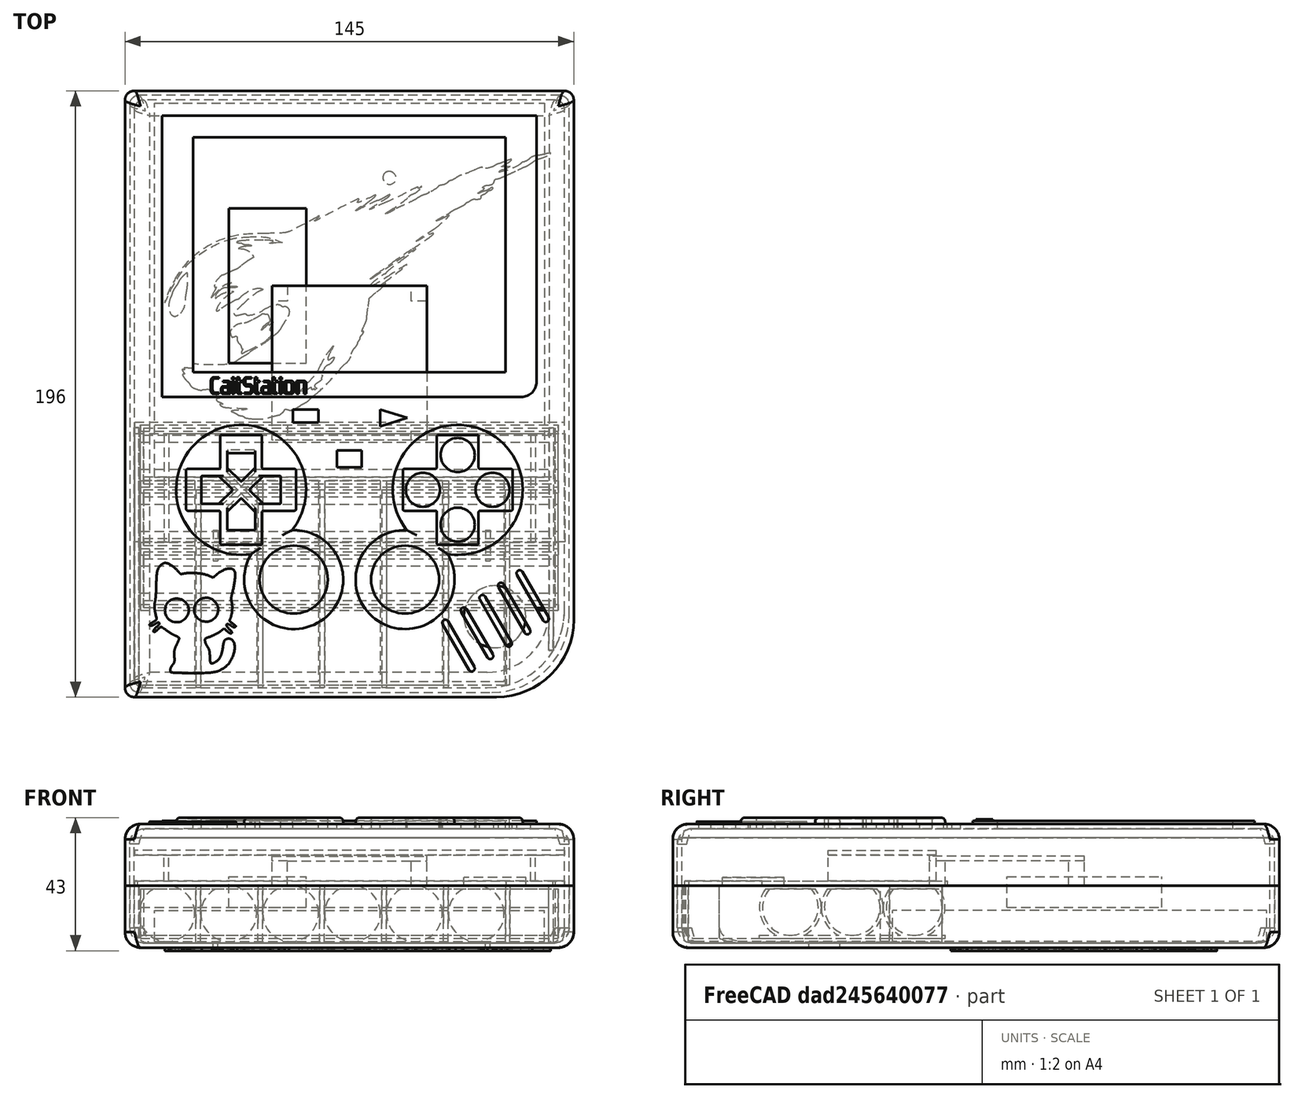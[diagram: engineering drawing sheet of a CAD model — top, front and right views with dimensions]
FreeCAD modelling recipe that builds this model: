
FCSTD DOCUMENT  (FreeCAD 0.15R4671 (Git))
Label: ps2-gb-small
License: All rights reserved
LicenseURL: http://en.wikipedia.org/wiki/All_rights_reserved
objects: Sketcher::SketchObject×33, PartDesign::Pad×32, Part::Cut×24, Part::MultiFuse×15, App::DocumentObjectGroup×15, PartDesign::Fillet×10, Part::Cylinder×9, Part::Feature×8, Part::Extrusion×6, Part::Box×5, Part::FeaturePython×2, Part::Part2DObjectPython×1
note: 177 computed .brp shape members not serialized (recipe doc carries the construction recipe); baked Part::Feature solids carry a one-line shape summary decoded from their .brp

FEATURE [Sketcher::SketchObject] Sketch001  label="Face-sketch"
  sketch-geometry (13):
    g0: LineSegment StartX=-69.5 StartY=88 StartZ=0 EndX=69.5 EndY=88 EndZ=0
    g1: LineSegment StartX=72.5 StartY=85 StartZ=0 EndX=72.5 EndY=-83 EndZ=0
    g2: LineSegment StartX=47.5 StartY=-108 StartZ=0 EndX=-69.5 EndY=-108 EndZ=0
    g3: LineSegment StartX=-72.5 StartY=-105 StartZ=0 EndX=-72.5 EndY=85 EndZ=0
    g4: LineSegment StartX=-50.5 StartY=73 StartZ=0 EndX=50.5 EndY=73 EndZ=0
    g5: LineSegment StartX=50.5 StartY=73 StartZ=0 EndX=50.5 EndY=-3 EndZ=0
    g6: LineSegment StartX=50.5 StartY=-3 StartZ=0 EndX=-50.5 EndY=-3 EndZ=0
    g7: LineSegment StartX=-50.5 StartY=-3 StartZ=0 EndX=-50.5 EndY=73 EndZ=0
    g8: ArcOfCircle CenterX=47.5 CenterY=-83 CenterZ=0 NormalX=0 NormalY=0 NormalZ=1 Radius=25 StartAngle=4.71239 EndAngle=6.28319
    g9: ArcOfCircle CenterX=-69.5 CenterY=-105 CenterZ=0 NormalX=0 NormalY=0 NormalZ=1 Radius=3 StartAngle=3.14159 EndAngle=4.71239
    g10: ArcOfCircle CenterX=69.5 CenterY=85 CenterZ=0 NormalX=0 NormalY=0 NormalZ=1 Radius=3 StartAngle=0 EndAngle=1.5708
    g11: ArcOfCircle CenterX=-69.5 CenterY=85 CenterZ=0 NormalX=0 NormalY=0 NormalZ=1 Radius=3 StartAngle=1.5708 EndAngle=3.14159
    g12: GeomPoint [constr] X=-72.5 Y=88 Z=0
  constraints (34):
    c: Horizontal(g0)
    c: Horizontal(g2)
    c: Vertical(g1)
    c: Vertical(g3)
    c: Coincident(g4,g5)
    c: Coincident(g5,g6)
    c: Coincident(g6,g7)
    c: Coincident(g7,g4)
    c: Horizontal(g4)
    c: Horizontal(g6)
    c: Vertical(g5)
    c: Vertical(g7)
    c: DistanceX(g4) = 101
    c: DistanceY(g7) = 76
    c: Tangent(g1,g8) = 1.5708
    c: Tangent(g2,g8) = 1.5708
    c: Radius(g8) = 25
    c: Tangent(g2,g9) = 1.5708
    c: Tangent(g3,g9) = 1.5708
    c: Tangent(g0,g10) = 1.5708
    c: Tangent(g1,g10) = 1.5708
    c: Tangent(g0,g11) = 1.5708
    c: Tangent(g3,g11) = 1.5708
    c: Radius(g11) = 3
    c: Radius(g10) = 3
    c: Equal(g10,g9)
    c: DistanceY(g3) = 190
    c: DistanceX(g0) = 139
    c: DistanceX(g12,g0) = 3
    c: DistanceY(g12,g3) = -3
    c: DistanceX(g12,g4) = 22
    c: DistanceY(g4,g12) = 15
    c: DistanceX(g12) = -72.5
    c: DistanceY(g12) = 88
FEATURE [PartDesign::Pad] Pad  label="Face-pad"
  Length = 20
  Length2 = 100
  Sketch = -> Sketch001
  Type = 0
FEATURE [PartDesign::Fillet] Fillet  label="Face-fillet"
  Base = -> Pad [Edge10,Edge4,Edge22,Edge16]
  Radius = 5
FEATURE [Sketcher::SketchObject] Sketch002  label="Face-sketch001"
  Placement = pos=(0,0,-1.5) rot=(0,0,1;0rad)
  sketch-geometry (9):
    g0: LineSegment StartX=-68 StartY=86.5 StartZ=0 EndX=68 EndY=86.5 EndZ=0
    g1: LineSegment StartX=71 StartY=83.5 StartZ=0 EndX=71 EndY=-81.5 EndZ=0
    g2: LineSegment StartX=46 StartY=-106.5 StartZ=0 EndX=-68 EndY=-106.5 EndZ=0
    g3: LineSegment StartX=-71 StartY=-103.5 StartZ=0 EndX=-71 EndY=83.5 EndZ=0
    g4: ArcOfCircle CenterX=46 CenterY=-81.5 CenterZ=0 NormalX=0 NormalY=0 NormalZ=1 Radius=25 StartAngle=4.71239 EndAngle=6.28319
    g5: ArcOfCircle CenterX=-68 CenterY=-103.5 CenterZ=0 NormalX=0 NormalY=0 NormalZ=1 Radius=3 StartAngle=3.14159 EndAngle=4.71239
    g6: ArcOfCircle CenterX=68 CenterY=83.5 CenterZ=0 NormalX=0 NormalY=0 NormalZ=1 Radius=3 StartAngle=0 EndAngle=1.5708
    g7: ArcOfCircle CenterX=-68 CenterY=83.5 CenterZ=0 NormalX=0 NormalY=0 NormalZ=1 Radius=3 StartAngle=1.5708 EndAngle=3.14159
    g8: GeomPoint [constr] X=-71 Y=86.5 Z=0
  constraints (22):
    c: Horizontal(g0)
    c: Horizontal(g2)
    c: Vertical(g1)
    c: Vertical(g3)
    c: Tangent(g1,g4) = 1.5708
    c: Tangent(g2,g4) = 1.5708
    c: Radius(g4) = 25
    c: Tangent(g2,g5) = 1.5708
    c: Tangent(g3,g5) = 1.5708
    c: Tangent(g0,g6) = 1.5708
    c: Tangent(g1,g6) = 1.5708
    c: Tangent(g0,g7) = 1.5708
    c: Tangent(g3,g7) = 1.5708
    c: Radius(g7) = 3
    c: Radius(g6) = 3
    c: Equal(g6,g5)
    c: DistanceY(g3) = 187
    c: DistanceX(g0) = 136
    c: DistanceX(g8,g0) = 3
    c: DistanceY(g8,g3) = -3
    c: DistanceX(g8) = -71
    c: DistanceY(g8) = 86.5
FEATURE [PartDesign::Pad] Pad001  label="Face-cut"
  Length = 20
  Length2 = 100
  Placement = pos=(0,0,-1.5) rot=(0,0,1;0rad)
  Sketch = -> Sketch002
  Type = 0
FEATURE [PartDesign::Fillet] Fillet001  label="Face-cut-fillet"
  Base = -> Pad001 [Edge4,Edge10,Edge16,Edge22]
  Placement = pos=(0,0,-1.5) rot=(0,0,1;0rad)
  Radius = 5
FEATURE [Part::Cut] Cut  label="Face-filleted-cut"
  Base = -> Fillet
  Tool = -> Fillet001
FEATURE [Sketcher::SketchObject] Sketch011  label="Control circles crosses"
  Placement = pos=(0,0,1.8) rot=(0,0,1;0rad)
  sketch-geometry (25):
    g0: LineSegment StartX=-6.25 StartY=17.75 StartZ=0 EndX=6.25 EndY=17.75 EndZ=0
    g1: LineSegment StartX=6.75 StartY=17.25 StartZ=0 EndX=6.75 EndY=7.25 EndZ=0
    g2: LineSegment StartX=6.25 StartY=-17.75 StartZ=0 EndX=-6.25 EndY=-17.75 EndZ=0
    g3: LineSegment StartX=-6.75 StartY=-17.25 StartZ=0 EndX=-6.75 EndY=-7.25 EndZ=0
    g4: LineSegment StartX=-17.25 StartY=6.75 StartZ=0 EndX=-7.25 EndY=6.75 EndZ=0
    g5: LineSegment StartX=17.75 StartY=6.25 StartZ=0 EndX=17.75 EndY=-6.25 EndZ=0
    g6: LineSegment StartX=17.25 StartY=-6.75 StartZ=0 EndX=7.25 EndY=-6.75 EndZ=0
    g7: LineSegment StartX=-17.75 StartY=-6.25 StartZ=0 EndX=-17.75 EndY=6.25 EndZ=0
    g8: LineSegment StartX=7.25 StartY=6.75 StartZ=0 EndX=17.25 EndY=6.75 EndZ=0
    g9: LineSegment StartX=6.75 StartY=-7.25 StartZ=0 EndX=6.75 EndY=-17.25 EndZ=0
    g10: LineSegment StartX=-7.25 StartY=-6.75 StartZ=0 EndX=-17.25 EndY=-6.75 EndZ=0
    g11: LineSegment StartX=-6.75 StartY=7.25 StartZ=0 EndX=-6.75 EndY=17.25 EndZ=0
    g12: ArcOfCircle CenterX=-6.25 CenterY=17.25 CenterZ=0 NormalX=0 NormalY=0 NormalZ=1 Radius=0.5 StartAngle=1.5708 EndAngle=3.14159
    g13: ArcOfCircle CenterX=6.25 CenterY=17.25 CenterZ=0 NormalX=0 NormalY=0 NormalZ=1 Radius=0.5 StartAngle=0 EndAngle=1.5708
    g14: ArcOfCircle CenterX=7.25 CenterY=7.25 CenterZ=0 NormalX=0 NormalY=0 NormalZ=1 Radius=0.5 StartAngle=3.14159 EndAngle=4.71239
    g15: ArcOfCircle CenterX=17.25 CenterY=6.25 CenterZ=0 NormalX=0 NormalY=0 NormalZ=1 Radius=0.5 StartAngle=0 EndAngle=1.5708
    g16: ArcOfCircle CenterX=17.25 CenterY=-6.25 CenterZ=0 NormalX=0 NormalY=0 NormalZ=1 Radius=0.5 StartAngle=4.71239 EndAngle=6.28319
    g17: ArcOfCircle CenterX=7.25 CenterY=-7.25 CenterZ=0 NormalX=0 NormalY=0 NormalZ=1 Radius=0.5 StartAngle=1.5708 EndAngle=3.14159
    g18: ArcOfCircle CenterX=6.25 CenterY=-17.25 CenterZ=0 NormalX=0 NormalY=0 NormalZ=1 Radius=0.5 StartAngle=4.71239 EndAngle=6.28319
    g19: ArcOfCircle CenterX=-6.25 CenterY=-17.25 CenterZ=0 NormalX=0 NormalY=0 NormalZ=1 Radius=0.5 StartAngle=3.14159 EndAngle=4.71239
    g20: ArcOfCircle CenterX=-7.25 CenterY=-7.25 CenterZ=0 NormalX=0 NormalY=0 NormalZ=1 Radius=0.5 StartAngle=0 EndAngle=1.5708
    g21: ArcOfCircle CenterX=-17.25 CenterY=-6.25 CenterZ=0 NormalX=0 NormalY=0 NormalZ=1 Radius=0.5 StartAngle=3.14159 EndAngle=4.71239
    g22: ArcOfCircle CenterX=-17.25 CenterY=6.25 CenterZ=0 NormalX=0 NormalY=0 NormalZ=1 Radius=0.5 StartAngle=1.5708 EndAngle=3.14159
    g23: ArcOfCircle CenterX=-7.25 CenterY=7.25 CenterZ=0 NormalX=0 NormalY=0 NormalZ=1 Radius=0.5 StartAngle=4.71239 EndAngle=6.28319
    g24: GeomPoint [constr] X=0 Y=0 Z=0
  constraints (53):
    c: Vertical(g5)
    c: Vertical(g7)
    c: Vertical(g1)
    c: Vertical(g11)
    c: Vertical(g9)
    c: Vertical(g3)
    c: Horizontal(g6)
    c: Horizontal(g10)
    c: Horizontal(g2)
    c: Horizontal(g4)
    c: Horizontal(g0)
    c: Horizontal(g8)
    c: Tangent(g0,g12) = 1.5708
    c: Tangent(g11,g12) = 1.5708
    c: Tangent(g0,g13) = 1.5708
    c: Tangent(g1,g13) = 1.5708
    c: Tangent(g1,g14) = -1.5708
    c: Tangent(g8,g14) = -1.5708
    c: Tangent(g8,g15) = 1.5708
    c: Tangent(g5,g15) = 1.5708
    c: Tangent(g5,g16) = 1.5708
    c: Tangent(g6,g16) = 1.5708
    c: Tangent(g6,g17) = -1.5708
    c: Tangent(g9,g17) = -1.5708
    c: Tangent(g9,g18) = 1.5708
    c: Tangent(g2,g18) = 1.5708
    c: Tangent(g2,g19) = 1.5708
    c: Tangent(g3,g19) = 1.5708
    c: Tangent(g10,g20) = -1.5708
    c: Tangent(g3,g20) = -1.5708
    c: Tangent(g10,g21) = 1.5708
    c: Tangent(g7,g21) = 1.5708
    c: Tangent(g7,g22) = 1.5708
    c: Tangent(g4,g22) = 1.5708
    c: Tangent(g4,g23) = -1.5708
    c: Tangent(g11,g23) = -1.5708
    c: Radius(g12) = 0.5
    c: Equal(g12, g13-g23) x11
    c: Equal(g11,g1)
    c: Equal(g1,g8)
    c: Equal(g8,g6)
    c: Equal(g6,g9)
    c: Equal(g9,g3)
    c: Equal(g3,g10)
    c: Equal(g10,g4)
    c: DistanceY(g1) = -10
    c: Equal(g0,g5)
    c: Equal(g5,g2)
    c: Equal(g2,g7)
    c: DistanceX(g0) = 12.5
    c: DistanceY(g24,g0) = 17.75
    c: DistanceX(g0,g24) = 6.25
    c: Coincident(g24,g-1)
FEATURE [Sketcher::SketchObject] Sketch012  label="Control circles triangles"
  Placement = pos=(0,0,3.6) rot=(0,0,1;0rad)
  sketch-geometry (15):
    g0: LineSegment StartX=0 StartY=16 StartZ=0 EndX=-1.75 EndY=14.25 EndZ=0
    g1: LineSegment StartX=-1.75 StartY=14.25 StartZ=0 EndX=1.75 EndY=14.25 EndZ=0
    g2: LineSegment StartX=1.75 StartY=14.25 StartZ=0 EndX=0 EndY=16 EndZ=0
    g3: LineSegment StartX=-14.25 StartY=1.75 StartZ=0 EndX=-14.25 EndY=-1.75 EndZ=0
    g4: LineSegment StartX=-14.25 StartY=-1.75 StartZ=0 EndX=-16 EndY=0 EndZ=0
    g5: LineSegment StartX=-16 StartY=0 StartZ=0 EndX=-14.25 EndY=1.75 EndZ=0
    g6: LineSegment StartX=14.25 StartY=1.75 StartZ=0 EndX=14.25 EndY=-1.75 EndZ=0
    g7: LineSegment StartX=14.25 StartY=-1.75 StartZ=0 EndX=16 EndY=0 EndZ=0
    g8: LineSegment StartX=16 StartY=0 StartZ=0 EndX=14.25 EndY=1.75 EndZ=0
    g9: LineSegment StartX=-1.75 StartY=-14.25 StartZ=0 EndX=1.75 EndY=-14.25 EndZ=0
    g10: LineSegment StartX=1.75 StartY=-14.25 StartZ=0 EndX=0 EndY=-16 EndZ=0
    g11: LineSegment StartX=0 StartY=-16 StartZ=0 EndX=-1.75 EndY=-14.25 EndZ=0
    g12: LineSegment [constr] StartX=0 StartY=16 StartZ=0 EndX=0 EndY=-16 EndZ=0
    g13: LineSegment [constr] StartX=-16 StartY=0 StartZ=0 EndX=16 EndY=0 EndZ=0
    g14: GeomPoint [constr] X=0 Y=0 Z=0
  constraints (41):
    c: Coincident(g1,g0)
    c: Horizontal(g1)
    c: Coincident(g2,g1)
    c: Coincident(g2,g0)
    c: Angle(g0,g2) = 1.5708
    c: Equal(g0,g2)
    c: DistanceX(g1) = 3.5
    c: Vertical(g3)
    c: Coincident(g3,g4)
    c: Coincident(g4,g5)
    c: Coincident(g5,g3)
    c: Vertical(g6)
    c: Coincident(g6,g7)
    c: Coincident(g7,g8)
    c: Coincident(g8,g6)
    c: Horizontal(g9)
    c: Coincident(g9,g10)
    c: Coincident(g10,g11)
    c: Coincident(g11,g9)
    c: Angle(g4,g5) = 1.5708
    c: Equal(g5,g4)
    c: DistanceY(g3) = -3.5
    c: Equal(g8,g7)
    c: Equal(g10,g11)
    c: DistanceX(g9) = 3.5
    c: DistanceY(g6) = -3.5
    c: Angle(g10,g11) = 1.5708
    c: Angle(g8,g7) = 1.5708
    c: DistanceX(g9,g0) = 0
    c: DistanceY(g3,g6) = 0
    c: Coincident(g12,g0)
    c: Coincident(g12,g10)
    c: Coincident(g13,g4)
    c: Coincident(g13,g7)
    c: PointOnObject(g14,g12)
    c: PointOnObject(g14,g13)
    c: DistanceX(g14,g4) = -16
    c: DistanceX(g14,g7) = 16
    c: DistanceY(g0,g14) = -16
    c: DistanceY(g14,g10) = -16
    c: Coincident(g14,g-1)
FEATURE [PartDesign::Pad] Pad009  label="Control circles crosses pad"
  Length = 1
  Length2 = 100
  Placement = pos=(0,0,1.8) rot=(0,0,1;0rad)
  Sketch = -> Sketch011
  Type = 0
FEATURE [PartDesign::Pad] Pad010  label="Control circles triangles pad"
  Length = 1
  Length2 = 100
  Placement = pos=(0,0,3.6) rot=(0,0,1;0rad)
  Sketch = -> Sketch012
  Type = 0
FEATURE [Sketcher::SketchObject] Sketch015  label="Button holes"
  sketch-geometry (44):
    g0: LineSegment StartX=-4.25 StartY=11.8232 StartZ=0 EndX=4.25 EndY=11.8232 EndZ=0
    g1: LineSegment StartX=4.5 StartY=11.5732 StartZ=0 EndX=4.5 EndY=7.25 EndZ=0
    g2: LineSegment StartX=-4.5 StartY=7.25 StartZ=0 EndX=-4.5 EndY=11.5732 EndZ=0
    g3: LineSegment StartX=-4.42678 StartY=7.07322 StartZ=0 EndX=-0.176777 EndY=2.82322 EndZ=0
    g4: LineSegment StartX=0.176777 StartY=2.82322 StartZ=0 EndX=4.42678 EndY=7.07322 EndZ=0
    g5: LineSegment StartX=-4.25 StartY=-13 StartZ=0 EndX=4.25 EndY=-13 EndZ=0
    g6: LineSegment StartX=4.5 StartY=-12.75 StartZ=0 EndX=4.5 EndY=-7.25 EndZ=0
    g7: LineSegment StartX=4.42678 StartY=-7.07322 StartZ=0 EndX=0.176777 EndY=-2.82322 EndZ=0
    g8: LineSegment StartX=-0.176777 StartY=-2.82322 StartZ=0 EndX=-4.42678 EndY=-7.07322 EndZ=0
    g9: LineSegment StartX=-4.5 StartY=-7.25 StartZ=0 EndX=-4.5 EndY=-12.75 EndZ=0
    g10: LineSegment StartX=7.25 StartY=4.5 StartZ=0 EndX=12.5732 EndY=4.5 EndZ=0
    g11: LineSegment StartX=12.8232 StartY=4.25 StartZ=0 EndX=12.8232 EndY=-4.25 EndZ=0
    g12: LineSegment StartX=12.5732 StartY=-4.5 StartZ=0 EndX=7.25 EndY=-4.5 EndZ=0
    g13: LineSegment StartX=7.07322 StartY=-4.42678 StartZ=0 EndX=2.82322 EndY=-0.176777 EndZ=0
    g14: LineSegment StartX=2.82322 StartY=0.176777 StartZ=0 EndX=7.07322 EndY=4.42678 EndZ=0
    g15: LineSegment StartX=-12.8232 StartY=4.25 StartZ=0 EndX=-12.8232 EndY=-4.25 EndZ=0
    g16: LineSegment StartX=-12.5732 StartY=-4.5 StartZ=0 EndX=-7.25 EndY=-4.5 EndZ=0
    g17: LineSegment StartX=-7.07322 StartY=-4.42678 StartZ=0 EndX=-2.82322 EndY=-0.176777 EndZ=0
    g18: LineSegment StartX=-2.82322 StartY=0.176777 StartZ=0 EndX=-7.07322 EndY=4.42678 EndZ=0
    g19: LineSegment StartX=-7.25 StartY=4.5 StartZ=0 EndX=-12.5732 EndY=4.5 EndZ=0
    g20: LineSegment [constr] StartX=0 StartY=3 StartZ=0 EndX=0 EndY=0 EndZ=0
    g21: LineSegment [constr] StartX=0 StartY=0 StartZ=0 EndX=0 EndY=-3 EndZ=0
    g22: LineSegment [constr] StartX=-3 StartY=0 StartZ=0 EndX=0 EndY=0 EndZ=0
    g23: LineSegment [constr] StartX=0 StartY=0 StartZ=0 EndX=3 EndY=0 EndZ=0
    g24: ArcOfCircle CenterX=4.25 CenterY=11.5732 CenterZ=0 NormalX=0 NormalY=0 NormalZ=1 Radius=0.25 StartAngle=0 EndAngle=1.5708
    g25: ArcOfCircle CenterX=4.25 CenterY=7.25 CenterZ=0 NormalX=0 NormalY=0 NormalZ=1 Radius=0.25 StartAngle=5.49779 EndAngle=6.28319
    g26: ArcOfCircle CenterX=0 CenterY=3 CenterZ=0 NormalX=0 NormalY=0 NormalZ=1 Radius=0.25 StartAngle=3.92699 EndAngle=5.49779
    g27: ArcOfCircle CenterX=-4.25 CenterY=7.25 CenterZ=0 NormalX=0 NormalY=0 NormalZ=1 Radius=0.25 StartAngle=3.14159 EndAngle=3.92699
    g28: ArcOfCircle CenterX=-4.25 CenterY=11.5732 CenterZ=0 NormalX=0 NormalY=0 NormalZ=1 Radius=0.25 StartAngle=1.5708 EndAngle=3.14159
    g29: ArcOfCircle CenterX=-7.25 CenterY=4.25 CenterZ=0 NormalX=0 NormalY=0 NormalZ=1 Radius=0.25 StartAngle=0.785398 EndAngle=1.5708
    g30: ArcOfCircle CenterX=-12.5732 CenterY=4.25 CenterZ=0 NormalX=0 NormalY=0 NormalZ=1 Radius=0.25 StartAngle=1.5708 EndAngle=3.14159
    g31: ArcOfCircle CenterX=-12.5732 CenterY=-4.25 CenterZ=0 NormalX=0 NormalY=0 NormalZ=1 Radius=0.25 StartAngle=3.14159 EndAngle=4.71239
    g32: ArcOfCircle CenterX=-7.25 CenterY=-4.25 CenterZ=0 NormalX=0 NormalY=0 NormalZ=1 Radius=0.25 StartAngle=4.71239 EndAngle=5.49779
    g33: ArcOfCircle CenterX=-3 CenterY=0 CenterZ=0 NormalX=0 NormalY=0 NormalZ=1 Radius=0.25 StartAngle=5.49779 EndAngle=7.06858
    g34: ArcOfCircle CenterX=0 CenterY=-3 CenterZ=0 NormalX=0 NormalY=0 NormalZ=1 Radius=0.25 StartAngle=0.785398 EndAngle=2.35619
    g35: ArcOfCircle CenterX=-4.25 CenterY=-7.25 CenterZ=0 NormalX=0 NormalY=0 NormalZ=1 Radius=0.25 StartAngle=2.35619 EndAngle=3.14159
    g36: ArcOfCircle CenterX=-4.25 CenterY=-12.75 CenterZ=0 NormalX=0 NormalY=0 NormalZ=1 Radius=0.25 StartAngle=3.14159 EndAngle=4.71239
    g37: ArcOfCircle CenterX=4.25 CenterY=-12.75 CenterZ=0 NormalX=0 NormalY=0 NormalZ=1 Radius=0.25 StartAngle=4.71239 EndAngle=6.28319
    g38: ArcOfCircle CenterX=4.25 CenterY=-7.25 CenterZ=0 NormalX=0 NormalY=0 NormalZ=1 Radius=0.25 StartAngle=0 EndAngle=0.785398
    g39: ArcOfCircle CenterX=3 CenterY=0 CenterZ=0 NormalX=0 NormalY=0 NormalZ=1 Radius=0.25 StartAngle=2.35619 EndAngle=3.92699
    g40: ArcOfCircle CenterX=7.25 CenterY=-4.25 CenterZ=0 NormalX=0 NormalY=0 NormalZ=1 Radius=0.25 StartAngle=3.92699 EndAngle=4.71239
    g41: ArcOfCircle CenterX=12.5732 CenterY=-4.25 CenterZ=0 NormalX=0 NormalY=0 NormalZ=1 Radius=0.25 StartAngle=4.71239 EndAngle=6.28319
    g42: ArcOfCircle CenterX=12.5732 CenterY=4.25 CenterZ=0 NormalX=0 NormalY=0 NormalZ=1 Radius=0.25 StartAngle=0 EndAngle=1.5708
    g43: ArcOfCircle CenterX=7.25 CenterY=4.25 CenterZ=0 NormalX=0 NormalY=0 NormalZ=1 Radius=0.25 StartAngle=1.5708 EndAngle=2.35619
  constraints (92):
    c: Horizontal(g0)
    c: Vertical(g1)
    c: Vertical(g2)
    c: Equal(g4,g3)
    c: Equal(g2,g1)
    c: Angle(g4,g3) = 1.5708
    c: Horizontal(g5)
    c: Vertical(g6)
    c: Vertical(g9)
    c: Horizontal(g10)
    c: Vertical(g11)
    c: Horizontal(g12)
    c: Vertical(g15)
    c: Horizontal(g16)
    c: Horizontal(g19)
    c: Equal(g18,g17)
    c: Equal(g8,g7)
    c: Equal(g14,g13)
    c: Equal(g10,g12)
    c: Equal(g6,g9)
    c: Equal(g19,g16)
    c: Angle(g18,g17) = 1.5708
    c: Angle(g13,g14) = 1.5708
    c: Angle(g8,g7) = 1.5708
    c: Equal(g5,g11)
    c: Equal(g11,g15)
    c: Equal(g15,g0)
    c: DistanceY(g22,g23) = 0
    c: Vertical(g20)
    c: Coincident(g21,g20)
    c: Vertical(g21)
    c: Horizontal(g22)
    c: Coincident(g23,g22)
    c: Coincident(g22,g20)
    c: DistanceX(g23) = 3
    c: DistanceX(g22) = 3
    c: DistanceY(g20) = -3
    c: DistanceY(g21) = -3
    c: Coincident(g20,g-1)
    c: Tangent(g0,g24) = 1.5708
    c: Tangent(g1,g24) = 1.5708
    c: Tangent(g1,g25) = 1.5708
    c: Tangent(g4,g25) = -1.5708
    c: Tangent(g4,g26) = -1.5708
    c: Tangent(g3,g26) = -1.5708
    c: Tangent(g3,g27) = -1.5708
    c: Tangent(g2,g27) = 1.5708
    c: Coincident(g28,g0)
    c: Coincident(g28,g2)
    c: DistanceY(g0,g4) = -9
    c: Coincident(g26,g20)
    c: Tangent(g18,g29) = -1.5708
    c: Tangent(g19,g29) = -1.5708
    c: Tangent(g19,g30) = -1.5708
    c: Tangent(g15,g30) = -1.5708
    c: Tangent(g15,g31) = -1.5708
    c: Tangent(g16,g31) = -1.5708
    c: Tangent(g16,g32) = -1.5708
    c: Tangent(g17,g32) = -1.5708
    c: Tangent(g18,g33) = -1.5708
    c: Tangent(g17,g33) = -1.5708
    c: Tangent(g7,g34) = -1.5708
    c: Tangent(g8,g34) = -1.5708
    c: Tangent(g8,g35) = -1.5708
    c: Tangent(g9,g35) = -1.5708
    c: Tangent(g9,g36) = -1.5708
    c: Tangent(g5,g36) = -1.5708
    c: Tangent(g5,g37) = -1.5708
    c: Tangent(g6,g37) = -1.5708
    c: Tangent(g6,g38) = -1.5708
    c: Tangent(g7,g38) = -1.5708
    c: Tangent(g14,g39) = 1.5708
    c: Tangent(g13,g39) = 1.5708
    c: Tangent(g13,g40) = 1.5708
    c: Tangent(g12,g40) = 1.5708
    c: Tangent(g12,g41) = 1.5708
    c: Tangent(g11,g41) = 1.5708
    c: Tangent(g11,g42) = 1.5708
    c: Tangent(g10,g42) = 1.5708
    c: Tangent(g10,g43) = 1.5708
    c: Tangent(g14,g43) = 1.5708
    c: Radius(g24) = 0.25
    c: Equal(g24, g25-g43) x19
    c: DistanceX(g2,g1) = 9
    c: Coincident(g22,g33)
    c: Coincident(g39,g23)
    c: Coincident(g21,g34)
    c: DistanceY(g5,g21) = 10
    c: DistanceX(g15,g18) = 10
    c: DistanceX(g14,g11) = 10
    c: Angle(g28) = 1.5708
    c: DistanceX(g0) = 8.5
FEATURE [PartDesign::Pad] Pad013  label="Button holes pad"
  Length = 10
  Length2 = 100
  Sketch = -> Sketch015
  Type = 0
FEATURE [Sketcher::SketchObject] Sketch019  label="Face button holes001"
  sketch-geometry (4):
    g0: Circle CenterX=0 CenterY=11.25 CenterZ=0 NormalX=0 NormalY=0 NormalZ=1 Radius=5.5
    g1: Circle CenterX=11.25 CenterY=0 CenterZ=0 NormalX=0 NormalY=0 NormalZ=1 Radius=5.5
    g2: Circle CenterX=0 CenterY=-11.25 CenterZ=0 NormalX=0 NormalY=0 NormalZ=1 Radius=5.5
    g3: Circle CenterX=-11.25 CenterY=0 CenterZ=0 NormalX=0 NormalY=0 NormalZ=1 Radius=5.5
  constraints (12):
    c: PointOnObject(g0,g-2)
    c: PointOnObject(g1,g-1)
    c: PointOnObject(g2,g-2)
    c: PointOnObject(g3,g-1)
    c: Radius(g3) = 5.5
    c: Equal(g3,g0)
    c: Equal(g3,g1)
    c: Equal(g3,g2)
    c: DistanceY(g0,g2) = -22.5
    c: DistanceX(g1,g3) = -22.5
    c: DistanceX(g-1,g1) = 11.25
    c: DistanceY(g-1,g0) = 11.25
FEATURE [PartDesign::Pad] Pad017  label="Face button holes pad001"
  Length = 10
  Length2 = 100
  Sketch = -> Sketch019
  Type = 0
FEATURE [Sketcher::SketchObject] Sketch020  label="Analog hole outline"
  Placement = pos=(-18,-70,20) rot=(0,0,1;0rad)
  sketch-geometry (2):
    g0: Circle CenterX=0 CenterY=0 CenterZ=0 NormalX=0 NormalY=0 NormalZ=1 Radius=16
    g1: Circle CenterX=0 CenterY=0 CenterZ=0 NormalX=0 NormalY=0 NormalZ=1 Radius=11
  constraints (4):
    c: Radius(g0) = 16
    c: Coincident(g0,g-1)
    c: Coincident(g1,g-1)
    c: Radius(g1) = 11
FEATURE [PartDesign::Pad] Pad018  label="Left Analog hole pad"
  Length = 2
  Length2 = 100
  Placement = pos=(-18,-70,20) rot=(0,0,1;0rad)
  Sketch = -> Sketch020
  Type = 0
FEATURE [Sketcher::SketchObject] Sketch026  label="StartSelect001"
  Placement = pos=(0,0,10) rot=(0,0,1;0rad)
  sketch-geometry (11):
    g0: LineSegment StartX=-18.25 StartY=-15 StartZ=0 EndX=-10 EndY=-15 EndZ=0
    g1: LineSegment StartX=-10 StartY=-15 StartZ=0 EndX=-10 EndY=-19.25 EndZ=0
    g2: LineSegment StartX=-10 StartY=-19.25 StartZ=0 EndX=-18.25 EndY=-19.25 EndZ=0
    g3: LineSegment StartX=-18.25 StartY=-19.25 StartZ=0 EndX=-18.25 EndY=-15 EndZ=0
    g4: LineSegment StartX=10 StartY=-15 StartZ=0 EndX=10 EndY=-20.5 EndZ=0
    g5: LineSegment StartX=10 StartY=-20.5 StartZ=0 EndX=18.75 EndY=-17.75 EndZ=0
    g6: LineSegment StartX=18.75 StartY=-17.75 StartZ=0 EndX=10 EndY=-15 EndZ=0
    g7: LineSegment StartX=-4 StartY=-28.25 StartZ=0 EndX=4 EndY=-28.25 EndZ=0
    g8: LineSegment StartX=4 StartY=-28.25 StartZ=0 EndX=4 EndY=-33.75 EndZ=0
    g9: LineSegment StartX=4 StartY=-33.75 StartZ=0 EndX=-4 EndY=-33.75 EndZ=0
    g10: LineSegment StartX=-4 StartY=-33.75 StartZ=0 EndX=-4 EndY=-28.25 EndZ=0
  constraints (33):
    c: Coincident(g0,g1)
    c: Coincident(g1,g2)
    c: Coincident(g2,g3)
    c: Coincident(g3,g0)
    c: Horizontal(g0)
    c: Horizontal(g2)
    c: Vertical(g1)
    c: Vertical(g3)
    c: Vertical(g4)
    c: Coincident(g4,g5)
    c: Coincident(g5,g6)
    c: Coincident(g6,g4)
    c: Equal(g5,g6)
    c: DistanceX(g4,g5) = 8.75
    c: DistanceY(g4,g4) = -5.5
    c: DistanceX(g0) = 8.25
    c: DistanceY(g3) = 4.25
    c: DistanceY(g4,g0) = 0
    c: DistanceX(g0) = -10
    c: DistanceY(g0) = -15
    c: DistanceX(g4) = 10
    c: Coincident(g7,g8)
    c: Coincident(g8,g9)
    c: Coincident(g9,g10)
    c: Coincident(g10,g7)
    c: Horizontal(g7)
    c: Horizontal(g9)
    c: Vertical(g8)
    c: Vertical(g10)
    c: DistanceY(g10) = 5.5
    c: DistanceX(g7) = 8
    c: DistanceX(g-1,g7) = 4
    c: DistanceY(g7,g1) = 9
FEATURE [PartDesign::Pad] Pad023  label="StartSelect Pad001"
  Length = 10
  Length2 = 100
  Placement = pos=(0,0,10) rot=(0,0,1;0rad)
  Sketch = -> Sketch026
  Type = 0
FEATURE [Part::Cut] Cut012
  Base = -> Cut
  Tool = -> Pad023
FEATURE [Sketcher::SketchObject] Sketch027  label="Face button holes002"
  Placement = pos=(35,-41,15) rot=(0,0,1;0rad)
  sketch-geometry (4):
    g0: Circle CenterX=0 CenterY=11.25 CenterZ=0 NormalX=0 NormalY=0 NormalZ=1 Radius=5.5
    g1: Circle CenterX=11.25 CenterY=0 CenterZ=0 NormalX=0 NormalY=0 NormalZ=1 Radius=5.5
    g2: Circle CenterX=0 CenterY=-11.25 CenterZ=0 NormalX=0 NormalY=0 NormalZ=1 Radius=5.5
    g3: Circle CenterX=-11.25 CenterY=0 CenterZ=0 NormalX=0 NormalY=0 NormalZ=1 Radius=5.5
  constraints (12):
    c: PointOnObject(g0,g-2)
    c: PointOnObject(g1,g-1)
    c: PointOnObject(g2,g-2)
    c: PointOnObject(g3,g-1)
    c: Radius(g3) = 5.5
    c: Equal(g3,g0)
    c: Equal(g3,g1)
    c: Equal(g3,g2)
    c: DistanceY(g0,g2) = -22.5
    c: DistanceX(g1,g3) = -22.5
    c: DistanceX(g-1,g1) = 11.25
    c: DistanceY(g-1,g0) = 11.25
FEATURE [PartDesign::Pad] Pad024  label="Face button holes pad002"
  Length = 10
  Length2 = 100
  Placement = pos=(35,-41,15) rot=(0,0,1;0rad)
  Sketch = -> Sketch027
  Type = 0
FEATURE [Sketcher::SketchObject] Sketch028  label="Dpad button holes"
  Placement = pos=(-35,-41,14) rot=(0,0,1;0rad)
  sketch-geometry (44):
    g0: LineSegment StartX=-4.25 StartY=12.8232 StartZ=0 EndX=4.25 EndY=12.8232 EndZ=0
    g1: LineSegment StartX=4.5 StartY=12.5732 StartZ=0 EndX=4.5 EndY=5.75 EndZ=0
    g2: LineSegment StartX=-4.5 StartY=5.75 StartZ=0 EndX=-4.5 EndY=12.5732 EndZ=0
    g3: LineSegment StartX=-4.42678 StartY=5.57322 StartZ=0 EndX=-0.176777 EndY=1.32322 EndZ=0
    g4: LineSegment StartX=0.176777 StartY=1.32322 StartZ=0 EndX=4.42678 EndY=5.57322 EndZ=0
    g5: LineSegment StartX=-4.25 StartY=-13 StartZ=0 EndX=4.25 EndY=-13 EndZ=0
    g6: LineSegment StartX=4.5 StartY=-12.75 StartZ=0 EndX=4.5 EndY=-5.75 EndZ=0
    g7: LineSegment StartX=4.42678 StartY=-5.57322 StartZ=0 EndX=0.176777 EndY=-1.32322 EndZ=0
    g8: LineSegment StartX=-0.176777 StartY=-1.32322 StartZ=0 EndX=-4.42678 EndY=-5.57322 EndZ=0
    g9: LineSegment StartX=-4.5 StartY=-5.75 StartZ=0 EndX=-4.5 EndY=-12.75 EndZ=0
    g10: LineSegment StartX=5.75 StartY=4.5 StartZ=0 EndX=12.5732 EndY=4.5 EndZ=0
    g11: LineSegment StartX=12.8232 StartY=4.25 StartZ=0 EndX=12.8232 EndY=-4.25 EndZ=0
    g12: LineSegment StartX=12.5732 StartY=-4.5 StartZ=0 EndX=5.75 EndY=-4.5 EndZ=0
    g13: LineSegment StartX=5.57322 StartY=-4.42678 StartZ=0 EndX=1.32322 EndY=-0.176777 EndZ=0
    g14: LineSegment StartX=1.32322 StartY=0.176777 StartZ=0 EndX=5.57322 EndY=4.42678 EndZ=0
    g15: LineSegment StartX=-12.8232 StartY=4.25 StartZ=0 EndX=-12.8232 EndY=-4.25 EndZ=0
    g16: LineSegment StartX=-12.5732 StartY=-4.5 StartZ=0 EndX=-5.75 EndY=-4.5 EndZ=0
    g17: LineSegment StartX=-5.57322 StartY=-4.42678 StartZ=0 EndX=-1.32322 EndY=-0.176777 EndZ=0
    g18: LineSegment StartX=-1.32322 StartY=0.176777 StartZ=0 EndX=-5.57322 EndY=4.42678 EndZ=0
    g19: LineSegment StartX=-5.75 StartY=4.5 StartZ=0 EndX=-12.5732 EndY=4.5 EndZ=0
    g20: LineSegment [constr] StartX=0 StartY=1.5 StartZ=0 EndX=0 EndY=0 EndZ=0
    g21: LineSegment [constr] StartX=0 StartY=0 StartZ=0 EndX=0 EndY=-1.5 EndZ=0
    g22: LineSegment [constr] StartX=-1.5 StartY=0 StartZ=0 EndX=0 EndY=0 EndZ=0
    g23: LineSegment [constr] StartX=0 StartY=0 StartZ=0 EndX=1.5 EndY=0 EndZ=0
    g24: ArcOfCircle CenterX=4.25 CenterY=12.5732 CenterZ=0 NormalX=0 NormalY=0 NormalZ=1 Radius=0.25 StartAngle=0 EndAngle=1.5708
    g25: ArcOfCircle CenterX=4.25 CenterY=5.75 CenterZ=0 NormalX=0 NormalY=0 NormalZ=1 Radius=0.25 StartAngle=5.49779 EndAngle=6.28319
    g26: ArcOfCircle CenterX=0 CenterY=1.5 CenterZ=0 NormalX=0 NormalY=0 NormalZ=1 Radius=0.25 StartAngle=3.92699 EndAngle=5.49779
    g27: ArcOfCircle CenterX=-4.25 CenterY=5.75 CenterZ=0 NormalX=0 NormalY=0 NormalZ=1 Radius=0.25 StartAngle=3.14159 EndAngle=3.92699
    g28: ArcOfCircle CenterX=-4.25 CenterY=12.5732 CenterZ=0 NormalX=0 NormalY=0 NormalZ=1 Radius=0.25 StartAngle=1.5708 EndAngle=3.14159
    g29: ArcOfCircle CenterX=-5.75 CenterY=4.25 CenterZ=0 NormalX=0 NormalY=0 NormalZ=1 Radius=0.25 StartAngle=0.785398 EndAngle=1.5708
    g30: ArcOfCircle CenterX=-12.5732 CenterY=4.25 CenterZ=0 NormalX=0 NormalY=0 NormalZ=1 Radius=0.25 StartAngle=1.5708 EndAngle=3.14159
    g31: ArcOfCircle CenterX=-12.5732 CenterY=-4.25 CenterZ=0 NormalX=0 NormalY=0 NormalZ=1 Radius=0.25 StartAngle=3.14159 EndAngle=4.71239
    g32: ArcOfCircle CenterX=-5.75 CenterY=-4.25 CenterZ=0 NormalX=0 NormalY=0 NormalZ=1 Radius=0.25 StartAngle=4.71239 EndAngle=5.49779
    g33: ArcOfCircle CenterX=-1.5 CenterY=0 CenterZ=0 NormalX=0 NormalY=0 NormalZ=1 Radius=0.25 StartAngle=5.49779 EndAngle=7.06858
    g34: ArcOfCircle CenterX=0 CenterY=-1.5 CenterZ=0 NormalX=0 NormalY=0 NormalZ=1 Radius=0.25 StartAngle=0.785398 EndAngle=2.35619
    g35: ArcOfCircle CenterX=-4.25 CenterY=-5.75 CenterZ=0 NormalX=0 NormalY=0 NormalZ=1 Radius=0.25 StartAngle=2.35619 EndAngle=3.14159
    g36: ArcOfCircle CenterX=-4.25 CenterY=-12.75 CenterZ=0 NormalX=0 NormalY=0 NormalZ=1 Radius=0.25 StartAngle=3.14159 EndAngle=4.71239
    g37: ArcOfCircle CenterX=4.25 CenterY=-12.75 CenterZ=0 NormalX=0 NormalY=0 NormalZ=1 Radius=0.25 StartAngle=4.71239 EndAngle=6.28319
    g38: ArcOfCircle CenterX=4.25 CenterY=-5.75 CenterZ=0 NormalX=0 NormalY=0 NormalZ=1 Radius=0.25 StartAngle=0 EndAngle=0.785398
    g39: ArcOfCircle CenterX=1.5 CenterY=0 CenterZ=0 NormalX=0 NormalY=0 NormalZ=1 Radius=0.25 StartAngle=2.35619 EndAngle=3.92699
    g40: ArcOfCircle CenterX=5.75 CenterY=-4.25 CenterZ=0 NormalX=0 NormalY=0 NormalZ=1 Radius=0.25 StartAngle=3.92699 EndAngle=4.71239
    g41: ArcOfCircle CenterX=12.5732 CenterY=-4.25 CenterZ=0 NormalX=0 NormalY=0 NormalZ=1 Radius=0.25 StartAngle=4.71239 EndAngle=6.28319
    g42: ArcOfCircle CenterX=12.5732 CenterY=4.25 CenterZ=0 NormalX=0 NormalY=0 NormalZ=1 Radius=0.25 StartAngle=0 EndAngle=1.5708
    g43: ArcOfCircle CenterX=5.75 CenterY=4.25 CenterZ=0 NormalX=0 NormalY=0 NormalZ=1 Radius=0.25 StartAngle=1.5708 EndAngle=2.35619
  constraints (92):
    c: Horizontal(g0)
    c: Vertical(g1)
    c: Vertical(g2)
    c: Equal(g4,g3)
    c: Equal(g2,g1)
    c: Angle(g4,g3) = 1.5708
    c: Horizontal(g5)
    c: Vertical(g6)
    c: Vertical(g9)
    c: Horizontal(g10)
    c: Vertical(g11)
    c: Horizontal(g12)
    c: Vertical(g15)
    c: Horizontal(g16)
    c: Horizontal(g19)
    c: Equal(g18,g17)
    c: Equal(g8,g7)
    c: Equal(g14,g13)
    c: Equal(g10,g12)
    c: Equal(g6,g9)
    c: Equal(g19,g16)
    c: Angle(g18,g17) = 1.5708
    c: Angle(g13,g14) = 1.5708
    c: Angle(g8,g7) = 1.5708
    c: Equal(g5,g11)
    c: Equal(g11,g15)
    c: Equal(g15,g0)
    c: DistanceY(g22,g23) = 0
    c: Vertical(g20)
    c: Coincident(g21,g20)
    c: Vertical(g21)
    c: Horizontal(g22)
    c: Coincident(g23,g22)
    c: Coincident(g22,g20)
    c: DistanceX(g23) = 1.5
    c: DistanceX(g22) = 1.5
    c: DistanceY(g20) = -1.5
    c: DistanceY(g21) = -1.5
    c: Coincident(g20,g-1)
    c: Tangent(g0,g24) = 1.5708
    c: Tangent(g1,g24) = 1.5708
    c: Tangent(g1,g25) = 1.5708
    c: Tangent(g4,g25) = -1.5708
    c: Tangent(g4,g26) = -1.5708
    c: Tangent(g3,g26) = -1.5708
    c: Tangent(g3,g27) = -1.5708
    c: Tangent(g2,g27) = 1.5708
    c: Coincident(g28,g0)
    c: Coincident(g28,g2)
    c: DistanceY(g0,g4) = -11.5
    c: Coincident(g26,g20)
    c: Tangent(g18,g29) = -1.5708
    c: Tangent(g19,g29) = -1.5708
    c: Tangent(g19,g30) = -1.5708
    c: Tangent(g15,g30) = -1.5708
    c: Tangent(g15,g31) = -1.5708
    c: Tangent(g16,g31) = -1.5708
    c: Tangent(g16,g32) = -1.5708
    c: Tangent(g17,g32) = -1.5708
    c: Tangent(g18,g33) = -1.5708
    c: Tangent(g17,g33) = -1.5708
    c: Tangent(g7,g34) = -1.5708
    c: Tangent(g8,g34) = -1.5708
    c: Tangent(g8,g35) = -1.5708
    c: Tangent(g9,g35) = -1.5708
    c: Tangent(g9,g36) = -1.5708
    c: Tangent(g5,g36) = -1.5708
    c: Tangent(g5,g37) = -1.5708
    c: Tangent(g6,g37) = -1.5708
    c: Tangent(g6,g38) = -1.5708
    c: Tangent(g7,g38) = -1.5708
    c: Tangent(g14,g39) = 1.5708
    c: Tangent(g13,g39) = 1.5708
    c: Tangent(g13,g40) = 1.5708
    c: Tangent(g12,g40) = 1.5708
    c: Tangent(g12,g41) = 1.5708
    c: Tangent(g11,g41) = 1.5708
    c: Tangent(g11,g42) = 1.5708
    c: Tangent(g10,g42) = 1.5708
    c: Tangent(g10,g43) = 1.5708
    c: Tangent(g14,g43) = 1.5708
    c: Radius(g24) = 0.25
    c: Equal(g24, g25-g43) x19
    c: DistanceX(g2,g1) = 9
    c: Coincident(g22,g33)
    c: Coincident(g39,g23)
    c: Coincident(g21,g34)
    c: DistanceY(g5,g21) = 11.5
    c: DistanceX(g15,g18) = 11.5
    c: DistanceX(g14,g11) = 11.5
    c: Angle(g28) = 1.5708
    c: DistanceX(g0) = 8.5
FEATURE [PartDesign::Pad] Pad025  label="Button holes pad003"
  Length = 10
  Length2 = 100
  Placement = pos=(-35,-41,14) rot=(0,0,1;0rad)
  Sketch = -> Sketch028
  Type = 0
FEATURE [Part::Cut] Cut013
  Base = -> Cut012
  Tool = -> Pad024
FEATURE [Part::Cut] Cut014
  Base = -> Cut013
  Tool = -> Pad025
FEATURE [Sketcher::SketchObject] Sketch030  label="Analog-cut-sketch"
  Placement = pos=(-18,-70,10) rot=(0,0,1;0rad)
  sketch-geometry (1):
    g0: Circle CenterX=0 CenterY=0 CenterZ=0 NormalX=0 NormalY=0 NormalZ=1 Radius=11
  constraints (2):
    c: Coincident(g0,g-1)
    c: Radius(g0) = 11
FEATURE [PartDesign::Pad] Pad035  label="Analog-cut-left"
  Length = 50
  Length2 = 100
  Placement = pos=(-18,-70,10) rot=(0,0,1;0rad)
  Sketch = -> Sketch030
  Type = 0
FEATURE [Sketcher::SketchObject] Sketch031  label="Analog-cut-sketch001"
  Placement = pos=(18,-70,10) rot=(0,0,1;0rad)
  sketch-geometry (1):
    g0: Circle CenterX=0 CenterY=0 CenterZ=0 NormalX=0 NormalY=0 NormalZ=1 Radius=11
  constraints (2):
    c: Coincident(g0,g-1)
    c: Radius(g0) = 11
FEATURE [PartDesign::Pad] Pad036  label="Analog-cut-right"
  Length = 50
  Length2 = 100
  Placement = pos=(18,-70,10) rot=(0,0,1;0rad)
  Sketch = -> Sketch031
  Type = 0
FEATURE [Part::Cut] Cut016
  Base = -> Cut014
  Tool = -> Pad035
FEATURE [Part::Cut] Cut017  label="Face-cut-ithink"
  Base = -> Cut016
  Tool = -> Pad036
FEATURE [Sketcher::SketchObject] Sketch032  label="Vent-sketch"
  Placement = pos=(37,-90,10) rot=(0,0,1;0rad)
  sketch-geometry (6):
    g0: LineSegment StartX=-6.86603 StartY=5.5 StartZ=0 EndX=1.63397 EndY=-9.22243 EndZ=0
    g1: ArcOfCircle CenterX=-6 CenterY=6 CenterZ=0 NormalX=0 NormalY=0 NormalZ=1 Radius=1 StartAngle=0.523599 EndAngle=3.66519
    g2: ArcOfCircle CenterX=2.5 CenterY=-8.72243 CenterZ=0 NormalX=0 NormalY=0 NormalZ=1 Radius=1 StartAngle=3.66519 EndAngle=6.80678
    g3: LineSegment StartX=-5.13397 StartY=6.5 StartZ=0 EndX=3.36603 EndY=-8.22243 EndZ=0
    g4: LineSegment [constr] StartX=3.36603 StartY=-8.22243 StartZ=0 EndX=1.63397 EndY=-9.22243 EndZ=0
    g5: LineSegment [constr] StartX=-5.13397 StartY=6.5 StartZ=0 EndX=-6.86603 EndY=5.5 EndZ=0
  constraints (18):
    c: Coincident(g1,g0)
    c: Coincident(g2,g0)
    c: Coincident(g3,g1)
    c: Coincident(g3,g2)
    c: Radius(g2) = 1
    c: Equal(g2,g1)
    c: Parallel(g3,g0)
    c: Coincident(g4,g2)
    c: Coincident(g4,g0)
    c: PointOnObject(g2,g4)
    c: Coincident(g5,g1)
    c: Coincident(g5,g0)
    c: PointOnObject(g1,g5)
    c: Angle(g0,g5) = 1.5708
    c: Angle(g0) = -1.0472
    c: DistanceX(g1) = -6
    c: DistanceY(g1) = 6
    c: Distance(g1,g2) = 17
FEATURE [PartDesign::Pad] Pad037  label="Vent"
  Length = 10
  Length2 = 100
  Placement = pos=(37,-90,10) rot=(0,0,1;0rad)
  Sketch = -> Sketch032
  Type = 0
FEATURE [Sketcher::SketchObject] Sketch033  label="Vent-sketch001"
  Placement = pos=(43,-86,10) rot=(0,0,1;0rad)
  sketch-geometry (6):
    g0: LineSegment StartX=-6.86603 StartY=5.5 StartZ=0 EndX=1.63398 EndY=-9.22244 EndZ=0
    g1: ArcOfCircle CenterX=-6 CenterY=6 CenterZ=0 NormalX=0 NormalY=0 NormalZ=1 Radius=1 StartAngle=0.523599 EndAngle=3.66519
    g2: ArcOfCircle CenterX=2.5 CenterY=-8.72243 CenterZ=0 NormalX=0 NormalY=0 NormalZ=1 Radius=1 StartAngle=3.66521 EndAngle=6.8068
    g3: LineSegment StartX=-5.13397 StartY=6.5 StartZ=0 EndX=3.36602 EndY=-8.22242 EndZ=0
    g4: LineSegment [constr] StartX=3.36602 StartY=-8.22242 StartZ=0 EndX=1.63398 EndY=-9.22244 EndZ=0
    g5: LineSegment [constr] StartX=-5.13397 StartY=6.5 StartZ=0 EndX=-6.86603 EndY=5.5 EndZ=0
  constraints (18):
    c: Coincident(g1,g0)
    c: Coincident(g2,g0)
    c: Coincident(g3,g1)
    c: Coincident(g3,g2)
    c: Radius(g2) = 1
    c: Equal(g2,g1)
    c: Parallel(g3,g0)
    c: Coincident(g4,g2)
    c: Coincident(g4,g0)
    c: PointOnObject(g2,g4)
    c: Coincident(g5,g1)
    c: Coincident(g5,g0)
    c: PointOnObject(g1,g5)
    c: Angle(g0,g5) = 1.5708
    c: Angle(g0) = -1.0472
    c: DistanceX(g1) = -6
    c: DistanceY(g1) = 6
    c: Distance(g1,g2) = 17
FEATURE [PartDesign::Pad] Pad038  label="Vent001"
  Length = 10
  Length2 = 100
  Placement = pos=(43,-86,10) rot=(0,0,1;0rad)
  Sketch = -> Sketch033
  Type = 0
FEATURE [Sketcher::SketchObject] Sketch034  label="Vent-sketch002"
  Placement = pos=(49,-82,10) rot=(0,0,1;0rad)
  sketch-geometry (6):
    g0: LineSegment StartX=-6.86603 StartY=5.5 StartZ=0 EndX=1.63398 EndY=-9.22244 EndZ=0
    g1: ArcOfCircle CenterX=-6 CenterY=6 CenterZ=0 NormalX=0 NormalY=0 NormalZ=1 Radius=1 StartAngle=0.523599 EndAngle=3.66519
    g2: ArcOfCircle CenterX=2.5 CenterY=-8.72243 CenterZ=0 NormalX=0 NormalY=0 NormalZ=1 Radius=1 StartAngle=3.66521 EndAngle=6.8068
    g3: LineSegment StartX=-5.13397 StartY=6.5 StartZ=0 EndX=3.36602 EndY=-8.22242 EndZ=0
    g4: LineSegment [constr] StartX=3.36602 StartY=-8.22242 StartZ=0 EndX=1.63398 EndY=-9.22244 EndZ=0
    g5: LineSegment [constr] StartX=-5.13397 StartY=6.5 StartZ=0 EndX=-6.86603 EndY=5.5 EndZ=0
  constraints (18):
    c: Coincident(g1,g0)
    c: Coincident(g2,g0)
    c: Coincident(g3,g1)
    c: Coincident(g3,g2)
    c: Radius(g2) = 1
    c: Equal(g2,g1)
    c: Parallel(g3,g0)
    c: Coincident(g4,g2)
    c: Coincident(g4,g0)
    c: PointOnObject(g2,g4)
    c: Coincident(g5,g1)
    c: Coincident(g5,g0)
    c: PointOnObject(g1,g5)
    c: Angle(g0,g5) = 1.5708
    c: Angle(g0) = -1.0472
    c: DistanceX(g1) = -6
    c: DistanceY(g1) = 6
    c: Distance(g2,g1) = 17
FEATURE [PartDesign::Pad] Pad039  label="Vent002"
  Length = 10
  Length2 = 100
  Placement = pos=(49,-82,10) rot=(0,0,1;0rad)
  Sketch = -> Sketch034
  Type = 0
FEATURE [Sketcher::SketchObject] Sketch035  label="Vent-sketch003"
  Placement = pos=(55,-78,10) rot=(0,0,1;0rad)
  sketch-geometry (6):
    g0: LineSegment StartX=-6.86603 StartY=5.5 StartZ=0 EndX=1.63397 EndY=-9.22243 EndZ=0
    g1: ArcOfCircle CenterX=-6 CenterY=6 CenterZ=0 NormalX=0 NormalY=0 NormalZ=1 Radius=1 StartAngle=0.523599 EndAngle=3.66519
    g2: ArcOfCircle CenterX=2.5 CenterY=-8.72243 CenterZ=0 NormalX=0 NormalY=0 NormalZ=1 Radius=1 StartAngle=3.66519 EndAngle=6.80678
    g3: LineSegment StartX=-5.13397 StartY=6.5 StartZ=0 EndX=3.36603 EndY=-8.22243 EndZ=0
    g4: LineSegment [constr] StartX=3.36603 StartY=-8.22243 StartZ=0 EndX=1.63397 EndY=-9.22243 EndZ=0
    g5: LineSegment [constr] StartX=-5.13397 StartY=6.5 StartZ=0 EndX=-6.86603 EndY=5.5 EndZ=0
  constraints (18):
    c: Coincident(g1,g0)
    c: Coincident(g2,g0)
    c: Coincident(g3,g1)
    c: Coincident(g3,g2)
    c: Radius(g2) = 1
    c: Equal(g2,g1)
    c: Parallel(g3,g0)
    c: Coincident(g4,g2)
    c: Coincident(g4,g0)
    c: PointOnObject(g2,g4)
    c: Coincident(g5,g1)
    c: Coincident(g5,g0)
    c: PointOnObject(g1,g5)
    c: Angle(g0,g5) = 1.5708
    c: Angle(g0) = -1.0472
    c: DistanceX(g1) = -6
    c: DistanceY(g1) = 6
    c: Distance(g1,g2) = 17
FEATURE [PartDesign::Pad] Pad040  label="Vent003"
  Length = 10
  Length2 = 100
  Placement = pos=(55,-78,10) rot=(0,0,1;0rad)
  Sketch = -> Sketch035
  Type = 0
FEATURE [Sketcher::SketchObject] Sketch036  label="Vent-sketch004"
  Placement = pos=(61,-74,10) rot=(0,0,1;0rad)
  sketch-geometry (6):
    g0: LineSegment StartX=-6.86603 StartY=5.5 StartZ=0 EndX=1.63398 EndY=-9.22244 EndZ=0
    g1: ArcOfCircle CenterX=-6 CenterY=6 CenterZ=0 NormalX=0 NormalY=0 NormalZ=1 Radius=1 StartAngle=0.523599 EndAngle=3.66519
    g2: ArcOfCircle CenterX=2.5 CenterY=-8.72243 CenterZ=0 NormalX=0 NormalY=0 NormalZ=1 Radius=1 StartAngle=3.66521 EndAngle=6.8068
    g3: LineSegment StartX=-5.13397 StartY=6.5 StartZ=0 EndX=3.36602 EndY=-8.22242 EndZ=0
    g4: LineSegment [constr] StartX=3.36602 StartY=-8.22242 StartZ=0 EndX=1.63398 EndY=-9.22244 EndZ=0
    g5: LineSegment [constr] StartX=-5.13397 StartY=6.5 StartZ=0 EndX=-6.86603 EndY=5.5 EndZ=0
  constraints (18):
    c: Coincident(g1,g0)
    c: Coincident(g2,g0)
    c: Coincident(g3,g1)
    c: Coincident(g3,g2)
    c: Radius(g2) = 1
    c: Equal(g2,g1)
    c: Parallel(g3,g0)
    c: Coincident(g4,g2)
    c: Coincident(g4,g0)
    c: PointOnObject(g2,g4)
    c: Coincident(g5,g1)
    c: Coincident(g5,g0)
    c: PointOnObject(g1,g5)
    c: Angle(g0,g5) = 1.5708
    c: Angle(g0) = -1.0472
    c: DistanceX(g1) = -6
    c: DistanceY(g1) = 6
    c: Distance(g1,g2) = 17
FEATURE [PartDesign::Pad] Pad041  label="Vent004"
  Length = 10
  Length2 = 100
  Placement = pos=(61,-74,10) rot=(0,0,1;0rad)
  Sketch = -> Sketch036
  Type = 0
FEATURE [Part::MultiFuse] Fusion
  Shapes = -> [Pad037,Pad038]
FEATURE [Part::MultiFuse] Fusion001
  Shapes = -> [Pad039,Fusion]
FEATURE [Part::MultiFuse] Fusion002
  Shapes = -> [Pad040,Fusion001]
FEATURE [Part::MultiFuse] Fusion003
  Shapes = -> [Pad041,Fusion002]
FEATURE [Part::Cut] Cut018  label="Face with vents"
  Base = -> Cut017
  Tool = -> Fusion003
FEATURE [Sketcher::SketchObject] Sketch037  label="Face-sketch002"
  Placement = pos=(0,0,-20) rot=(0,0,1;0rad)
  sketch-geometry (9):
    g0: LineSegment StartX=-69.5 StartY=88 StartZ=0 EndX=69.5 EndY=88 EndZ=0
    g1: LineSegment StartX=72.5 StartY=85 StartZ=0 EndX=72.5 EndY=-105 EndZ=0
    g2: LineSegment StartX=69.5 StartY=-108 StartZ=0 EndX=-47.5 EndY=-108 EndZ=0
    g3: LineSegment StartX=-72.5 StartY=-83 StartZ=0 EndX=-72.5 EndY=85 EndZ=0
    g4: ArcOfCircle CenterX=69.5 CenterY=-105 CenterZ=0 NormalX=0 NormalY=0 NormalZ=1 Radius=3 StartAngle=4.71239 EndAngle=6.28319
    g5: ArcOfCircle CenterX=-47.5 CenterY=-83 CenterZ=0 NormalX=0 NormalY=0 NormalZ=1 Radius=25 StartAngle=3.14159 EndAngle=4.71239
    g6: ArcOfCircle CenterX=69.5 CenterY=85 CenterZ=0 NormalX=0 NormalY=0 NormalZ=1 Radius=3 StartAngle=0 EndAngle=1.5708
    g7: ArcOfCircle CenterX=-69.5 CenterY=85 CenterZ=0 NormalX=0 NormalY=0 NormalZ=1 Radius=3 StartAngle=1.5708 EndAngle=3.14159
    g8: GeomPoint [constr] X=-72.5 Y=88 Z=0
  constraints (22):
    c: Horizontal(g0)
    c: Horizontal(g2)
    c: Vertical(g1)
    c: Vertical(g3)
    c: Tangent(g1,g4) = 1.5708
    c: Tangent(g2,g4) = 1.5708
    c: Tangent(g2,g5) = 1.5708
    c: Tangent(g3,g5) = 1.5708
    c: Tangent(g0,g6) = 1.5708
    c: Tangent(g1,g6) = 1.5708
    c: Tangent(g0,g7) = 1.5708
    c: Tangent(g3,g7) = 1.5708
    c: Radius(g7) = 3
    c: Radius(g6) = 3
    c: DistanceX(g0) = 139
    c: DistanceX(g8,g0) = 3
    c: DistanceY(g8,g3) = -3
    c: DistanceX(g8) = -72.5
    c: DistanceY(g8) = 88
    c: DistanceY(g1) = -190
    c: Radius(g5) = 25
    c: Equal(g4,g6)
FEATURE [PartDesign::Pad] Pad042  label="Face-pad001"
  Length = 20
  Length2 = 100
  Placement = pos=(0,0,-20) rot=(0,0,1;0rad)
  Sketch = -> Sketch037
  Type = 0
FEATURE [PartDesign::Fillet] Fillet008  label="Face-fillet001"
  Base = -> Pad042 [Edge10,Edge4,Edge22,Edge16]
  Placement = pos=(0,0,-20) rot=(0,0,1;0rad)
  Radius = 5
FEATURE [Sketcher::SketchObject] Sketch038  label="Face-sketch003"
  Placement = pos=(0,0,-21.5) rot=(0,0,1;0rad)
  sketch-geometry (9):
    g0: LineSegment StartX=-68 StartY=86.5 StartZ=0 EndX=68 EndY=86.5 EndZ=0
    g1: LineSegment StartX=71 StartY=83.5 StartZ=0 EndX=71 EndY=-103.5 EndZ=0
    g2: LineSegment StartX=68 StartY=-106.5 StartZ=0 EndX=-46 EndY=-106.5 EndZ=0
    g3: LineSegment StartX=-71 StartY=-81.5 StartZ=0 EndX=-71 EndY=83.5 EndZ=0
    g4: ArcOfCircle CenterX=68 CenterY=-103.5 CenterZ=0 NormalX=0 NormalY=0 NormalZ=1 Radius=3 StartAngle=4.71239 EndAngle=6.28319
    g5: ArcOfCircle CenterX=-46 CenterY=-81.5 CenterZ=0 NormalX=0 NormalY=0 NormalZ=1 Radius=25 StartAngle=3.14159 EndAngle=4.71239
    g6: ArcOfCircle CenterX=68 CenterY=83.5 CenterZ=0 NormalX=0 NormalY=0 NormalZ=1 Radius=3 StartAngle=0 EndAngle=1.5708
    g7: ArcOfCircle CenterX=-68 CenterY=83.5 CenterZ=0 NormalX=0 NormalY=0 NormalZ=1 Radius=3 StartAngle=1.5708 EndAngle=3.14159
    g8: GeomPoint [constr] X=-71 Y=86.5 Z=0
  constraints (22):
    c: Horizontal(g0)
    c: Horizontal(g2)
    c: Vertical(g1)
    c: Vertical(g3)
    c: Tangent(g1,g4) = 1.5708
    c: Tangent(g2,g4) = 1.5708
    c: Tangent(g2,g5) = 1.5708
    c: Tangent(g3,g5) = 1.5708
    c: Tangent(g0,g6) = 1.5708
    c: Tangent(g1,g6) = 1.5708
    c: Tangent(g0,g7) = 1.5708
    c: Tangent(g3,g7) = 1.5708
    c: Radius(g7) = 3
    c: Radius(g6) = 3
    c: DistanceX(g0) = 136
    c: DistanceX(g8,g0) = 3
    c: DistanceY(g8,g3) = -3
    c: DistanceX(g8) = -71
    c: DistanceY(g8) = 86.5
    c: DistanceY(g1) = -187
    c: Equal(g7,g4)
    c: Radius(g5) = 25
FEATURE [PartDesign::Pad] Pad043  label="Face-cut001"
  Length = 20
  Length2 = 100
  Placement = pos=(0,0,-21.5) rot=(0,0,1;0rad)
  Sketch = -> Sketch038
  Type = 0
FEATURE [PartDesign::Fillet] Fillet009  label="Face-cut-fillet001"
  Base = -> Pad043 [Edge4,Edge10,Edge16,Edge22]
  Placement = pos=(0,0,-21.5) rot=(0,0,1;0rad)
  Radius = 5
FEATURE [Part::Cut] Cut019  label="Back-filleted"
  Base = -> Fillet008
  Placement = pos=(0,0,-20) rot=(0,1,0;3.14159rad)
  Tool = -> Fillet009
FEATURE [Sketcher::SketchObject] Sketch039  label="Control circles sketch001"
  sketch-geometry (1):
    g0: Circle CenterX=0 CenterY=0 CenterZ=0 NormalX=0 NormalY=0 NormalZ=1 Radius=21
  constraints (2):
    c: Radius(g0) = 21
    c: Coincident(g0,g-1)
FEATURE [PartDesign::Pad] Pad044  label="Control cirlcles pad"
  Length = 2
  Length2 = 100
  Sketch = -> Sketch039
  Type = 0
FEATURE [PartDesign::Fillet] Fillet010  label="Control circles fillet"
  Base = -> Pad044 [Edge3]
  Radius = 1.2
FEATURE [Part::Cut] Cut020  label="Control circles cross cut"
  Base = -> Fillet010
  Tool = -> Pad009
FEATURE [Part::Cut] Cut021  label="Control circle cross triangle cut"
  Base = -> Cut020
  Tool = -> Pad010
FEATURE [Part::Cut] Cut022  label="Control dpad cut"
  Base = -> Cut021
  Placement = pos=(-35,-41,20) rot=(0,0,1;0rad)
  Tool = -> Pad013
FEATURE [Part::Cut] Cut023  label="Control face buttons cut001"
  Base = -> Cut020
  Placement = pos=(35,-41,20) rot=(0,0,1;0rad)
  Tool = -> Pad017
FEATURE [PartDesign::Fillet] Fillet011  label="Left Analog"
  Base = -> Pad018 [Edge3]
  Placement = pos=(-18,-70,20) rot=(0,0,1;0rad)
  Radius = 1.2
FEATURE [Sketcher::SketchObject] Sketch040  label="Analog hole outline001"
  Placement = pos=(18,-70,20) rot=(0,0,1;0rad)
  sketch-geometry (2):
    g0: Circle CenterX=0 CenterY=0 CenterZ=0 NormalX=0 NormalY=0 NormalZ=1 Radius=16
    g1: Circle CenterX=0 CenterY=0 CenterZ=0 NormalX=0 NormalY=0 NormalZ=1 Radius=11
  constraints (4):
    c: Radius(g0) = 16
    c: Coincident(g0,g-1)
    c: Coincident(g1,g-1)
    c: Radius(g1) = 11
FEATURE [PartDesign::Pad] Pad046  label="Right Analog hole pad"
  Length = 2
  Length2 = 100
  Placement = pos=(18,-70,20) rot=(0,0,1;0rad)
  Sketch = -> Sketch040
  Type = 0
FEATURE [App::DocumentObjectGroup] Group004  label="Analog"
  Group = -> [Pad018,Pad046]
FEATURE [PartDesign::Fillet] Fillet012  label="Right Analog"
  Base = -> Pad046 [Edge3]
  Placement = pos=(18,-70,20) rot=(0,0,1;0rad)
  Radius = 1.2
FEATURE [Part::MultiFuse] Fusion004  label="Face control extrusions"
  Shapes = -> [Fillet011,Fillet012,Cut022,Cut023]
FEATURE [Sketcher::SketchObject] Sketch041  label="Bezel sketch"
  Placement = pos=(0,0,8.8) rot=(0,0,1;0rad)
  sketch-geometry (5):
    g0: LineSegment StartX=-60.5 StartY=80 StartZ=0 EndX=60.5 EndY=80 EndZ=0
    g1: LineSegment StartX=60.5 StartY=80 StartZ=0 EndX=60.5 EndY=-6 EndZ=0
    g2: LineSegment StartX=55.5 StartY=-11 StartZ=0 EndX=-60.5 EndY=-11 EndZ=0
    g3: LineSegment StartX=-60.5 StartY=-11 StartZ=0 EndX=-60.5 EndY=80 EndZ=0
    g4: ArcOfCircle CenterX=55.5 CenterY=-6 CenterZ=0 NormalX=0 NormalY=0 NormalZ=1 Radius=5 StartAngle=4.71239 EndAngle=6.28319
  constraints (14):
    c: Coincident(g0,g1)
    c: Coincident(g2,g3)
    c: Coincident(g3,g0)
    c: Horizontal(g0)
    c: Horizontal(g2)
    c: Vertical(g1)
    c: Vertical(g3)
    c: DistanceX(g0) = 121
    c: DistanceY(g3) = 91
    c: Tangent(g1,g4) = 1.5708
    c: Tangent(g2,g4) = 1.5708
    c: Radius(g4) = 5
    c: DistanceY(g-1,g0) = 80
    c: DistanceX(g-1,g0) = -60.5
FEATURE [PartDesign::Pad] Pad047  label="Bezel pad"
  Length = 5
  Length2 = 100
  Placement = pos=(0,0,8.8) rot=(0,0,1;0rad)
  Sketch = -> Sketch041
  Type = 0
FEATURE [Part::Cut] Cut024  label="Face with bezel"
  Base = -> Cut018
  Tool = -> Pad047
FEATURE [Sketcher::SketchObject] Sketch042  label="Platform top"
  Placement = pos=(0,0,8) rot=(0,0,1;0rad)
  sketch-geometry (4):
    g0: LineSegment StartX=-25 StartY=25 StartZ=0 EndX=25 EndY=25 EndZ=0
    g1: LineSegment StartX=25 StartY=25 StartZ=0 EndX=25 EndY=-25 EndZ=0
    g2: LineSegment StartX=25 StartY=-25 StartZ=0 EndX=-25 EndY=-25 EndZ=0
    g3: LineSegment StartX=-25 StartY=-25 StartZ=0 EndX=-25 EndY=25 EndZ=0
  constraints (12):
    c: Coincident(g0,g1)
    c: Coincident(g1,g2)
    c: Coincident(g2,g3)
    c: Coincident(g3,g0)
    c: Horizontal(g0)
    c: Horizontal(g2)
    c: Vertical(g1)
    c: Vertical(g3)
    c: DistanceX(g0) = -25
    c: DistanceY(g0) = 25
    c: DistanceX(g0) = 50
    c: DistanceY(g3) = 50
FEATURE [Sketcher::SketchObject] Sketch043  label="Platform legs"
  sketch-geometry (16):
    g0: LineSegment StartX=-25 StartY=25 StartZ=0 EndX=-20 EndY=25 EndZ=0
    g1: LineSegment StartX=-20 StartY=25 StartZ=0 EndX=-20 EndY=20 EndZ=0
    g2: LineSegment StartX=-20 StartY=20 StartZ=0 EndX=-25 EndY=20 EndZ=0
    g3: LineSegment StartX=-25 StartY=20 StartZ=0 EndX=-25 EndY=25 EndZ=0
    g4: LineSegment StartX=20 StartY=25 StartZ=0 EndX=25 EndY=25 EndZ=0
    g5: LineSegment StartX=25 StartY=25 StartZ=0 EndX=25 EndY=20 EndZ=0
    g6: LineSegment StartX=25 StartY=20 StartZ=0 EndX=20 EndY=20 EndZ=0
    g7: LineSegment StartX=20 StartY=20 StartZ=0 EndX=20 EndY=25 EndZ=0
    g8: LineSegment StartX=-25 StartY=-20 StartZ=0 EndX=-20 EndY=-20 EndZ=0
    g9: LineSegment StartX=-20 StartY=-20 StartZ=0 EndX=-20 EndY=-25 EndZ=0
    g10: LineSegment StartX=-20 StartY=-25 StartZ=0 EndX=-25 EndY=-25 EndZ=0
    g11: LineSegment StartX=-25 StartY=-25 StartZ=0 EndX=-25 EndY=-20 EndZ=0
    g12: LineSegment StartX=20 StartY=-20 StartZ=0 EndX=25 EndY=-20 EndZ=0
    g13: LineSegment StartX=25 StartY=-20 StartZ=0 EndX=25 EndY=-25 EndZ=0
    g14: LineSegment StartX=25 StartY=-25 StartZ=0 EndX=20 EndY=-25 EndZ=0
    g15: LineSegment StartX=20 StartY=-25 StartZ=0 EndX=20 EndY=-20 EndZ=0
  constraints (48):
    c: Coincident(g0,g1)
    c: Coincident(g1,g2)
    c: Coincident(g2,g3)
    c: Coincident(g3,g0)
    c: Horizontal(g0)
    c: Horizontal(g2)
    c: Vertical(g1)
    c: Vertical(g3)
    c: DistanceX(g0) = -25
    c: DistanceY(g0) = 25
    c: DistanceY(g1) = -5
    c: Coincident(g4,g5)
    c: Coincident(g5,g6)
    c: Coincident(g6,g7)
    c: Coincident(g7,g4)
    c: Horizontal(g4)
    c: Horizontal(g6)
    c: Vertical(g5)
    c: Vertical(g7)
    c: Coincident(g8,g9)
    c: Coincident(g9,g10)
    c: Coincident(g10,g11)
    c: Coincident(g11,g8)
    c: Horizontal(g8)
    c: Horizontal(g10)
    c: Vertical(g9)
    c: Vertical(g11)
    c: Coincident(g12,g13)
    c: Coincident(g13,g14)
    c: Coincident(g14,g15)
    c: Coincident(g15,g12)
    c: Horizontal(g12)
    c: Horizontal(g14)
    c: Vertical(g13)
    c: Vertical(g15)
    c: Equal(g7,g12)
    c: Equal(g12,g15)
    c: Equal(g15,g9)
    c: Equal(g9,g8)
    c: Equal(g8,g2)
    c: Equal(g2,g1)
    c: Equal(g1,g6)
    c: DistanceX(g4) = 25
    c: DistanceY(g4) = 25
    c: DistanceX(g13) = 25
    c: DistanceY(g13) = -25
    c: DistanceX(g10) = -25
    c: DistanceY(g10) = -25
FEATURE [PartDesign::Pad] Pad048
  Length = 8
  Length2 = 100
  Sketch = -> Sketch043
  Type = 0
FEATURE [PartDesign::Pad] Pad049
  Length = 1.5
  Length2 = 100
  Placement = pos=(0,0,8) rot=(0,0,1;0rad)
  Sketch = -> Sketch042
  Type = 0
FEATURE [Part::MultiFuse] Fusion005
  Shapes = -> [Pad048,Pad049]
FEATURE [App::DocumentObjectGroup] Group007  label="Controls prototypes"
  Group = -> [Fusion005]
FEATURE [Part::Cylinder] Cylinder001  label="Cell001"
  Angle = 360
  Height = 65
  Placement = pos=(-59,-38,-9) rot=(1,0,0;1.5708rad)
  Radius = 9
FEATURE [Part::Cylinder] Cylinder002  label="Cell002"
  Angle = 360
  Height = 65
  Placement = pos=(-39,-38,-9) rot=(1,0,0;1.5708rad)
  Radius = 9
FEATURE [Part::Cylinder] Cylinder003  label="Cell003"
  Angle = 360
  Height = 65
  Placement = pos=(-19,-38,-9) rot=(1,0,0;1.5708rad)
  Radius = 9
FEATURE [Part::Cylinder] Cylinder004  label="Cell004"
  Angle = 360
  Height = 65
  Placement = pos=(1,-38,-9) rot=(1,0,0;1.5708rad)
  Radius = 9
FEATURE [Part::Cylinder] Cylinder005  label="Cell005"
  Angle = 360
  Height = 65
  Placement = pos=(21,-38,-9) rot=(1,0,0;1.5708rad)
  Radius = 9
FEATURE [Part::Cylinder] Cylinder006  label="Cell006"
  Angle = 360
  Height = 65
  Placement = pos=(41,-38,-9) rot=(1,0,0;1.5708rad)
  Radius = 9
FEATURE [App::DocumentObjectGroup] Group008  label="Cells"
  Group = -> [Cylinder001,Cylinder002,Cylinder003,Cylinder004,Cylinder005,Cylinder006]
FEATURE [Sketcher::SketchObject] Sketch  label="Mobo-sketch"
  Placement = pos=(0,26,-18) rot=(0,0,1;0rad)
  sketch-geometry (4):
    g0: LineSegment StartX=-63 StartY=58 StartZ=0 EndX=63 EndY=58 EndZ=0
    g1: LineSegment StartX=63 StartY=58 StartZ=0 EndX=63 EndY=-63 EndZ=0
    g2: LineSegment StartX=63 StartY=-63 StartZ=0 EndX=-63 EndY=-63 EndZ=0
    g3: LineSegment StartX=-63 StartY=-63 StartZ=0 EndX=-63 EndY=58 EndZ=0
  constraints (12):
    c: Coincident(g0,g1)
    c: Coincident(g1,g2)
    c: Coincident(g2,g3)
    c: Horizontal(g0)
    c: Horizontal(g2)
    c: Vertical(g1)
    c: Vertical(g3)
    c: DistanceY(g1) = -121
    c: DistanceX(g2) = -126
    c: DistanceX(g1) = 63
    c: DistanceY(g1) = -63
    c: Coincident(g3,g0)
FEATURE [Sketcher::SketchObject] Sketch044  label="Inner frame back sketch"
  Placement = pos=(0,0,-18.5) rot=(0,0,1;0rad)
  sketch-geometry (9):
    g0: LineSegment StartX=-68 StartY=86.5 StartZ=0 EndX=68 EndY=86.5 EndZ=0
    g1: LineSegment StartX=71 StartY=83.5 StartZ=0 EndX=71 EndY=-81.5 EndZ=0
    g2: LineSegment StartX=46 StartY=-106.5 StartZ=0 EndX=-68 EndY=-106.5 EndZ=0
    g3: LineSegment StartX=-71 StartY=-103.5 StartZ=0 EndX=-71 EndY=83.5 EndZ=0
    g4: ArcOfCircle CenterX=46 CenterY=-81.5 CenterZ=0 NormalX=0 NormalY=0 NormalZ=1 Radius=25 StartAngle=4.71239 EndAngle=6.28319
    g5: ArcOfCircle CenterX=-68 CenterY=-103.5 CenterZ=0 NormalX=0 NormalY=0 NormalZ=1 Radius=3 StartAngle=3.14159 EndAngle=4.71239
    g6: ArcOfCircle CenterX=68 CenterY=83.5 CenterZ=0 NormalX=0 NormalY=0 NormalZ=1 Radius=3 StartAngle=0 EndAngle=1.5708
    g7: ArcOfCircle CenterX=-68 CenterY=83.5 CenterZ=0 NormalX=0 NormalY=0 NormalZ=1 Radius=3 StartAngle=1.5708 EndAngle=3.14159
    g8: GeomPoint [constr] X=-71 Y=86.5 Z=0
  constraints (22):
    c: Horizontal(g0)
    c: Horizontal(g2)
    c: Vertical(g1)
    c: Vertical(g3)
    c: Tangent(g1,g4) = 1.5708
    c: Tangent(g2,g4) = 1.5708
    c: Tangent(g2,g5) = 1.5708
    c: Tangent(g3,g5) = 1.5708
    c: Tangent(g0,g6) = 1.5708
    c: Tangent(g1,g6) = 1.5708
    c: Tangent(g0,g7) = 1.5708
    c: Tangent(g3,g7) = 1.5708
    c: Radius(g7) = 3
    c: Radius(g6) = 3
    c: DistanceX(g0) = 136
    c: DistanceX(g8,g0) = 3
    c: DistanceY(g8,g3) = -3
    c: DistanceX(g8) = -71
    c: DistanceY(g8) = 86.5
    c: Radius(g4) = 25
    c: Equal(g5,g6)
    c: DistanceY(g3) = 187
FEATURE [PartDesign::Pad] Pad050  label="Inner frame back solid"
  Length = 34
  Length2 = 100
  Placement = pos=(0,0,-18.5) rot=(0,0,1;0rad)
  Sketch = -> Sketch044
  Type = 0
FEATURE [Sketcher::SketchObject] Sketch045  label="Inner frame back cut sketch"
  Placement = pos=(0,0,-18.5) rot=(0,0,1;0rad)
  sketch-geometry (9):
    g0: LineSegment StartX=-66.5 StartY=85 StartZ=0 EndX=66.5 EndY=85 EndZ=0
    g1: LineSegment StartX=69.5 StartY=82 StartZ=0 EndX=69.5 EndY=-80 EndZ=0
    g2: LineSegment StartX=44.5 StartY=-105 StartZ=0 EndX=-66.5 EndY=-105 EndZ=0
    g3: LineSegment StartX=-69.5 StartY=-102 StartZ=0 EndX=-69.5 EndY=82 EndZ=0
    g4: ArcOfCircle CenterX=44.5 CenterY=-80 CenterZ=0 NormalX=0 NormalY=0 NormalZ=1 Radius=25 StartAngle=4.71239 EndAngle=6.28319
    g5: ArcOfCircle CenterX=-66.5 CenterY=-102 CenterZ=0 NormalX=0 NormalY=0 NormalZ=1 Radius=3 StartAngle=3.14159 EndAngle=4.71239
    g6: ArcOfCircle CenterX=66.5 CenterY=82 CenterZ=0 NormalX=0 NormalY=0 NormalZ=1 Radius=3 StartAngle=0 EndAngle=1.5708
    g7: ArcOfCircle CenterX=-66.5 CenterY=82 CenterZ=0 NormalX=0 NormalY=0 NormalZ=1 Radius=3 StartAngle=1.5708 EndAngle=3.14159
    g8: GeomPoint [constr] X=-71 Y=86.5 Z=0
  constraints (22):
    c: Horizontal(g0)
    c: Horizontal(g2)
    c: Vertical(g1)
    c: Vertical(g3)
    c: Tangent(g1,g4) = 1.5708
    c: Tangent(g2,g4) = 1.5708
    c: Tangent(g2,g5) = 1.5708
    c: Tangent(g3,g5) = 1.5708
    c: Tangent(g0,g6) = 1.5708
    c: Tangent(g1,g6) = 1.5708
    c: Tangent(g0,g7) = 1.5708
    c: Tangent(g3,g7) = 1.5708
    c: Radius(g7) = 3
    c: Radius(g6) = 3
    c: DistanceX(g0) = 133
    c: DistanceX(g8,g0) = 4.5
    c: DistanceY(g8,g3) = -4.5
    c: DistanceX(g8) = -71
    c: DistanceY(g8) = 86.5
    c: DistanceY(g3) = 184
    c: Radius(g4) = 25
    c: Equal(g7,g5)
FEATURE [PartDesign::Pad] Pad051  label="Inner frame back cut solid"
  Length = 35.5
  Length2 = 100
  Placement = pos=(0,0,-18.5) rot=(0,0,1;0rad)
  Sketch = -> Sketch045
  Type = 0
FEATURE [App::DocumentObjectGroup] Group009  label="Inner frame back"
  Group = -> [Pad050,Pad051]
FEATURE [PartDesign::Fillet] Fillet013  label="Inner frame back fillet"
  Base = -> Pad050 [Edge15,Edge9,Edge3,Edge21]
  Placement = pos=(0,0,-18.5) rot=(0,0,1;0rad)
  Radius = 5
FEATURE [PartDesign::Fillet] Fillet014  label="Inner frame back cut fillet"
  Base = -> Pad051 [Edge3,Edge21,Edge15,Edge9]
  Placement = pos=(0,0,-18.5) rot=(0,0,1;0rad)
  Radius = 5
FEATURE [Part::Cut] Cut025  label="Inner frame walls"
  Base = -> Fillet013
  Tool = -> Fillet014
FEATURE [PartDesign::Pad] Pad052  label="mobo pad"
  Length = 10
  Length2 = 100
  Placement = pos=(0,26,-18) rot=(0,0,1;0rad)
  Sketch = -> Sketch
  Type = 0
FEATURE [Part::Box] Box  label="Heatsink"
  Height = 10
  Length = 25
  Placement = pos=(-39,0,-7) rot=(0,0,1;0rad)
  Width = 50
FEATURE [Part::MultiFuse] Fusion006  label="Motherboard"
  Shapes = -> [Pad052,Box]
FEATURE [Part::Cylinder] Cylinder  label="Speaker"
  Angle = 360
  Height = 2.75
  Placement = pos=(47,-82,0) rot=(0,0,1;0rad)
  Radius = 10
FEATURE [Part::Part2DObjectPython] ShapeString  # Draft 2D object (typed FeaturePython)
  FontFile = <userpath>/Downloads/playstation/zrnic___.ttf
  Placement = pos=(-45,-10,20) rot=(0,0,1;0rad)
  Size = 3
  String = CaitStation
  Tracking = 0
FEATURE [Sketcher::SketchObject] Sketch046  label="Bezel001"
  Placement = pos=(0,0,18.8) rot=(0,0,1;0rad)
  sketch-geometry (5):
    g0: LineSegment StartX=-60.5 StartY=80 StartZ=0 EndX=60.5 EndY=80 EndZ=0
    g1: LineSegment StartX=60.5 StartY=80 StartZ=0 EndX=60.5 EndY=-6 EndZ=0
    g2: LineSegment StartX=55.5 StartY=-11 StartZ=0 EndX=-60.5 EndY=-11 EndZ=0
    g3: LineSegment StartX=-60.5 StartY=-11 StartZ=0 EndX=-60.5 EndY=80 EndZ=0
    g4: ArcOfCircle CenterX=55.5 CenterY=-6 CenterZ=0 NormalX=0 NormalY=0 NormalZ=1 Radius=5 StartAngle=4.71239 EndAngle=6.28319
  constraints (14):
    c: Coincident(g0,g1)
    c: Coincident(g2,g3)
    c: Coincident(g3,g0)
    c: Horizontal(g0)
    c: Horizontal(g2)
    c: Vertical(g1)
    c: Vertical(g3)
    c: DistanceX(g0) = 121
    c: DistanceY(g3) = 91
    c: Tangent(g1,g4) = 1.5708
    c: Tangent(g2,g4) = 1.5708
    c: Radius(g4) = 5
    c: DistanceY(g-1,g0) = 80
    c: DistanceX(g-1,g0) = -60.5
FEATURE [PartDesign::Pad] Pad053  label="Bezel solid"
  Length = 1
  Length2 = 100
  Placement = pos=(0,0,18.8) rot=(0,0,1;0rad)
  Sketch = -> Sketch046
  Type = 0
FEATURE [Sketcher::SketchObject] Sketch047  label="Bezel cut sketch"
  sketch-geometry (4):
    g0: LineSegment StartX=-50.5 StartY=73 StartZ=0 EndX=50.5 EndY=73 EndZ=0
    g1: LineSegment StartX=50.5 StartY=73 StartZ=0 EndX=50.5 EndY=-3 EndZ=0
    g2: LineSegment StartX=50.5 StartY=-3 StartZ=0 EndX=-50.5 EndY=-3 EndZ=0
    g3: LineSegment StartX=-50.5 StartY=-3 StartZ=0 EndX=-50.5 EndY=73 EndZ=0
  constraints (12):
    c: Coincident(g0,g1)
    c: Coincident(g1,g2)
    c: Coincident(g2,g3)
    c: Coincident(g3,g0)
    c: Horizontal(g0)
    c: Horizontal(g2)
    c: Vertical(g1)
    c: Vertical(g3)
    c: DistanceX(g0) = 101
    c: DistanceY(g3) = 76
    c: DistanceX(g0) = -50.5
    c: DistanceY(g0) = 73
FEATURE [PartDesign::Pad] Pad054  label="Bezel cut solid"
  Length = 20
  Length2 = 100
  Sketch = -> Sketch047
  Type = 0
FEATURE [Part::Cut] Cut026  label="Bezel cut"
  Base = -> Pad053
  Tool = -> Pad054
FEATURE [PartDesign::Pad] Pad055  label="CaitStation"
  Length = 0.3
  Length2 = 100
  Placement = pos=(-45,-10,20) rot=(0,0,1;0rad)
  Sketch = -> ShapeString
  Type = 0
FEATURE [Part::MultiFuse] Fusion007  label="Bezel"
  Placement = pos=(0,0,1.2) rot=(0,0,1;0rad)
  Shapes = -> [Cut026,Pad055]
FEATURE [Part::Feature] Face  label="Face009"
  shape: bbox 112.1 x 142.5 x 2e-07 mm, 1 faces, 0 solids (baked)
FEATURE [Part::Feature] Face001  label="Face010"
  shape: bbox 31.3 x 34.42 x 2e-07 mm, 1 faces, 0 solids (baked)
FEATURE [Part::Feature] Face002  label="Face011"
  shape: bbox 35.55 x 34.37 x 2e-07 mm, 1 faces, 0 solids (baked)
FEATURE [Part::Cut] Cut027
  Base = -> Face
  Tool = -> Face001
FEATURE [Part::Cut] Cut028
  Base = -> Cut027
  Tool = -> Face002
FEATURE [Part::Extrusion] Extrude  label="Cat solid"
  Base = -> Cut028
  Dir = (0,0,3)
  Solid = false
FEATURE [Part::FeaturePython] Clone  label="Cat"  # Draft clone (typed FeaturePython)
  Objects = -> [Extrude]
  Placement = pos=(-69,-103,20) rot=(0,0,1;0rad)
  Scale = (0.25,0.25,0.25)
FEATURE [Part::Feature] Face003  label="Face012"
  shape: bbox 45.64 x 60.12 x 2e-07 mm, 1 faces, 0 solids (baked)
FEATURE [Part::Feature] Face004  label="Face013"
  shape: bbox 18.96 x 18.59 x 2e-07 mm, 1 faces, 0 solids (baked)
FEATURE [Part::Feature] Face005  label="Face014"
  shape: bbox 25.65 x 56.95 x 2e-07 mm, 1 faces, 0 solids (baked)
FEATURE [Part::Feature] Face006  label="Face015"
  shape: bbox 56.63 x 51.63 x 2e-07 mm, 1 faces, 0 solids (baked)
FEATURE [Part::Feature] Face007  label="Face016"
  shape: bbox 499.9 x 344.4 x 2e-07 mm, 1 faces, 0 solids (baked)
FEATURE [Part::Cut] Cut029
  Base = -> Face007
  Tool = -> Face003
FEATURE [Part::MultiFuse] Fusion008  label="Meteor full"
  Shapes = -> [Face004,Face006,Cut029,Face005]
FEATURE [Part::Extrusion] Extrude001  label="Meteor solid"
  Base = -> Fusion008
  Dir = (0,0,4)
  Solid = false
FEATURE [Part::FeaturePython] Clone001  label="Meteor"  # Draft clone (typed FeaturePython)
  Objects = -> [Extrude001]
  Placement = pos=(-71,-30,-21) rot=(0,0,1;0rad)
  Scale = (0.25,0.25,0.25)
FEATURE [Sketcher::SketchObject] Sketch048
  Placement = pos=(0,0,10) rot=(0,0,1;0rad)
  sketch-geometry (4):
    g0: LineSegment StartX=-69.3268 StartY=-22.8474 StartZ=0 EndX=69.6732 EndY=-22.8474 EndZ=0
    g1: LineSegment StartX=69.6732 StartY=-22.8474 StartZ=0 EndX=69.6732 EndY=-57.8474 EndZ=0
    g2: LineSegment StartX=69.6732 StartY=-57.8474 StartZ=0 EndX=-69.3268 EndY=-57.8474 EndZ=0
    g3: LineSegment StartX=-69.3268 StartY=-57.8474 StartZ=0 EndX=-69.3268 EndY=-22.8474 EndZ=0
  constraints (10):
    c: Coincident(g0,g1)
    c: Coincident(g1,g2)
    c: Coincident(g2,g3)
    c: Coincident(g3,g0)
    c: Horizontal(g0)
    c: Horizontal(g2)
    c: Vertical(g1)
    c: Vertical(g3)
    c: DistanceX(g0) = 139
    c: DistanceY(g1) = -35
FEATURE [Sketcher::SketchObject] Sketch049
  Placement = pos=(-0.75,0,0) rot=(0,0,1;0rad)
  sketch-geometry (16):
    g0: LineSegment StartX=-68.6077 StartY=-19.1615 StartZ=0 EndX=70.3923 EndY=-19.1615 EndZ=0
    g1: LineSegment StartX=70.3923 StartY=-19.1615 StartZ=0 EndX=70.3923 EndY=-79.1615 EndZ=0
    g2: LineSegment StartX=70.3923 StartY=-79.1615 StartZ=0 EndX=-68.6077 EndY=-79.1615 EndZ=0
    g3: LineSegment StartX=-68.6077 StartY=-79.1615 StartZ=0 EndX=-68.6077 EndY=-19.1615 EndZ=0
    g4: LineSegment StartX=-68.6077 StartY=-79.1615 StartZ=0 EndX=51.3923 EndY=-79.1615 EndZ=0
    g5: LineSegment StartX=51.3923 StartY=-79.1615 StartZ=0 EndX=51.3923 EndY=-104.162 EndZ=0
    g6: LineSegment StartX=51.3923 StartY=-104.162 StartZ=0 EndX=-68.6077 EndY=-104.162 EndZ=0
    g7: LineSegment StartX=-68.6077 StartY=-104.162 StartZ=0 EndX=-68.6077 EndY=-79.1615 EndZ=0
    g8: LineSegment StartX=70.3923 StartY=-79.1615 StartZ=0 EndX=66.5144 EndY=-79.1615 EndZ=0
    g9: LineSegment StartX=66.5144 StartY=-79.1615 StartZ=0 EndX=66.5144 EndY=-89.5113 EndZ=0
    g10: LineSegment StartX=66.5144 StartY=-89.5113 StartZ=0 EndX=70.3923 EndY=-89.5113 EndZ=0
    g11: LineSegment StartX=70.3923 StartY=-89.5113 StartZ=0 EndX=70.3923 EndY=-79.1615 EndZ=0
    g12: LineSegment StartX=66.5144 StartY=-89.5113 StartZ=0 EndX=68.6984 EndY=-89.5113 EndZ=0
    g13: LineSegment StartX=68.6984 StartY=-89.5113 StartZ=0 EndX=68.6984 EndY=-92.0336 EndZ=0
    g14: LineSegment StartX=68.6984 StartY=-92.0336 StartZ=0 EndX=66.5144 EndY=-92.0336 EndZ=0
    g15: LineSegment StartX=66.5144 StartY=-92.0336 StartZ=0 EndX=66.5144 EndY=-89.5113 EndZ=0
  constraints (40):
    c: Coincident(g0,g1)
    c: Coincident(g1,g2)
    c: Coincident(g2,g3)
    c: Coincident(g3,g0)
    c: Horizontal(g0)
    c: Horizontal(g2)
    c: Vertical(g1)
    c: Vertical(g3)
    c: DistanceX(g0) = 139
    c: DistanceY(g3) = 60
    c: Coincident(g4,g5)
    c: Coincident(g5,g6)
    c: Coincident(g6,g7)
    c: Coincident(g7,g4)
    c: Horizontal(g4)
    c: Horizontal(g6)
    c: Vertical(g5)
    c: Vertical(g7)
    c: PointOnObject(g4,g2)
    c: DistanceX(g6) = -120
    c: DistanceY(g7) = 25
    c: DistanceX(g4,g2) = 0
    c: Coincident(g8,g9)
    c: Coincident(g9,g10)
    c: Coincident(g10,g11)
    c: Coincident(g11,g8)
    c: Horizontal(g8)
    c: Horizontal(g10)
    c: Vertical(g9)
    c: Vertical(g11)
    c: Coincident(g8,g1)
    c: Coincident(g12,g13)
    c: Coincident(g13,g14)
    c: Coincident(g14,g15)
    c: Coincident(g15,g12)
    c: Horizontal(g12)
    c: Horizontal(g14)
    c: Vertical(g13)
    c: Vertical(g15)
    c: Coincident(g12,g9)
FEATURE [PartDesign::Pad] Pad056
  Length = 1.5
  Length2 = 100
  Placement = pos=(-0.75,0,0) rot=(0,0,1;0rad)
  Sketch = -> Sketch049
  Type = 0
FEATURE [Sketcher::SketchObject] Sketch050
  Placement = pos=(0,0,-18.5) rot=(0,0,1;0rad)
  sketch-geometry (9):
    g0: LineSegment StartX=-69.5927 StartY=-20.9105 StartZ=0 EndX=-69.5927 EndY=-105.911 EndZ=0
    g1: LineSegment StartX=30.4073 StartY=-40.9105 StartZ=0 EndX=30.4073 EndY=-105.911 EndZ=0
    g2: LineSegment StartX=10.4073 StartY=-40.9105 StartZ=0 EndX=10.4073 EndY=-105.911 EndZ=0
    g3: LineSegment StartX=-9.59269 StartY=-40.9105 StartZ=0 EndX=-9.59269 EndY=-105.911 EndZ=0
    g4: LineSegment StartX=-29.5927 StartY=-40.9105 StartZ=0 EndX=-29.5927 EndY=-105.911 EndZ=0
    g5: LineSegment StartX=-49.5927 StartY=-40.9105 StartZ=0 EndX=-49.5927 EndY=-105.911 EndZ=0
    g6: LineSegment [constr] StartX=65.4073 StartY=-105.911 StartZ=0 EndX=-69.5927 EndY=-105.911 EndZ=0
    g7: LineSegment StartX=50.4073 StartY=-105.911 StartZ=0 EndX=50.4073 EndY=-40.9105 EndZ=0
    g8: LineSegment StartX=64.4073 StartY=-20.9105 StartZ=0 EndX=64.4073 EndY=-92.9105 EndZ=0
  constraints (33):
    c: Vertical(g0)
    c: Vertical(g1)
    c: Vertical(g2)
    c: Vertical(g3)
    c: Vertical(g4)
    c: Vertical(g5)
    c: Coincident(g6,g0)
    c: Horizontal(g6)
    c: PointOnObject(g5,g6)
    c: PointOnObject(g4,g6)
    c: PointOnObject(g3,g6)
    c: PointOnObject(g2,g6)
    c: PointOnObject(g1,g6)
    c: Equal(g1,g2)
    c: Equal(g2,g3)
    c: Equal(g3,g4)
    c: Equal(g4,g5)
    c: DistanceY(g5) = -65
    c: DistanceX(g0,g5) = 20
    c: DistanceX(g5,g4) = 20
    c: DistanceX(g4,g3) = 20
    c: DistanceX(g3,g2) = 20
    c: DistanceX(g2,g1) = 20
    c: DistanceY(g0) = -85
    c: PointOnObject(g7,g6)
    c: Vertical(g7)
    c: Equal(g1,g7)
    c: DistanceX(g7,g1) = -20
    c: DistanceX(g7,g6) = 15
    c: Vertical(g8)
    c: DistanceX(g8,g0) = -134
    c: DistanceY(g8) = -72
    c: DistanceY(g8,g0) = 0
FEATURE [Part::Extrusion] Extrude002
  Base = -> Sketch050
  Dir = (0,0,18.5)
  Solid = false
FEATURE [Part::Extrusion] Extrude003
  Base = -> Extrude002
  Dir = (1.5,0,0)
  Solid = false
FEATURE [Part::MultiFuse] Fusion009
  Shapes = -> [Pad056,Extrude003]
FEATURE [Part::Cut] Cut030
  Base = -> Fusion009
  Tool = -> Cut019
FEATURE [Part::Cut] Cut031  label="First layer"
  Base = -> Cut030
  Tool = -> Cut025
FEATURE [PartDesign::Fillet] Fillet015  label="Insert"
  Base = -> Cut025 [Edge12,Edge16,Edge13,Edge3]
  Radius = 1.2
FEATURE [PartDesign::Pad] Pad057
  Length = 1.5
  Length2 = 100
  Placement = pos=(0,0,10) rot=(0,0,1;0rad)
  Sketch = -> Sketch048
  Type = 0
FEATURE [Sketcher::SketchObject] Sketch051
  Placement = pos=(0,0,1.5) rot=(0,0,1;0rad)
  sketch-geometry (2):
    g0: LineSegment StartX=-59.9264 StartY=-22.8115 StartZ=0 EndX=-59.9264 EndY=-57.8115 EndZ=0
    g1: LineSegment StartX=58.5736 StartY=-22.8115 StartZ=0 EndX=58.5736 EndY=-57.8115 EndZ=0
  constraints (6):
    c: Vertical(g0)
    c: Vertical(g1)
    c: DistanceX(g0,g1) = 118.5
    c: Equal(g1,g0)
    c: DistanceY(g1) = -35
    c: DistanceY(g1,g0) = 0
FEATURE [Part::Extrusion] Extrude004
  Base = -> Sketch051
  Dir = (0,0,8.5)
  Solid = false
FEATURE [Part::Extrusion] Extrude005
  Base = -> Extrude004
  Dir = (1.5,0,0)
  Solid = false
FEATURE [Part::MultiFuse] Fusion010  label="Second layer"
  Shapes = -> [Pad057,Extrude005]
FEATURE [App::DocumentObjectGroup] Group012  label="First layer controls and battery compartments"
  Group = -> [Cut031,Fusion010]
FEATURE [Part::Box] Box001  label="left button cable slit"
  Height = 10
  Length = 1.5
  Placement = pos=(-44,-64,-25) rot=(0,0,1;0rad)
  Width = 10
FEATURE [Part::Box] Box002  label="right button cable slit"
  Height = 10
  Length = 1.5
  Placement = pos=(44,-64,-25) rot=(0,0,1;0rad)
  Width = 10
FEATURE [Part::Cut] Cut032  label="Back-L1L2cut"
  Base = -> Cut019
  Tool = -> Box001
FEATURE [Part::Cut] Cut033  label="Back-R1R2cut"
  Base = -> Cut032
  Tool = -> Box002
FEATURE [App::DocumentObjectGroup] Group013  label="Construction"
  Group = -> [Pad001,Pad]
FEATURE [App::DocumentObjectGroup] Group  label="Face008"
  Group = -> [Cut024,Fusion007,Group013]
FEATURE [App::DocumentObjectGroup] Group014  label="Construction001"
  Group = -> [Cylinder,Fusion006,Group009,Group008,Group007]
FEATURE [App::DocumentObjectGroup] Group001  label="Internal components"
  Group = -> [Group014,Fillet015]
FEATURE [App::DocumentObjectGroup] Group015  label="Construction002"
  Group = -> [Pad044,Group004]
FEATURE [App::DocumentObjectGroup] Group003  label="Controls"
  Group = -> [Fusion004,Group015]
FEATURE [App::DocumentObjectGroup] Group016  label="Construction003"
FEATURE [App::DocumentObjectGroup] Group006  label="Back"
  Group = -> [Pad043,Pad042,Cut033,Group016]
FEATURE [App::DocumentObjectGroup] Group017  label="Construction004"
  Group = -> [Fusion008,Extrude001,Extrude]
FEATURE [App::DocumentObjectGroup] Group010  label="Flair"
  Group = -> [Clone,Clone001,Group017]
FEATURE [Part::Cylinder] Cylinder007  label="Battery holder volume"
  Angle = 360
  Height = 135
  Placement = pos=(0,0,0) rot=(0,1,0;1.5708rad)
  Radius = 10
FEATURE [Part::Cylinder] Cylinder008  label="Battery holder inner volume"
  Angle = 360
  Height = 133
  Placement = pos=(1,0,0) rot=(0,1,0;1.5708rad)
  Radius = 9
FEATURE [Part::Cut] Cut034
  Base = -> Cylinder007
  Tool = -> Cylinder008
FEATURE [Part::Box] Box003  label="Cube"
  Height = 20
  Length = 135
  Placement = pos=(0,-10,6) rot=(0,0,1;0rad)
  Width = 20
FEATURE [Part::Cut] Cut035
  Base = -> Cut034
  Tool = -> Box003
FEATURE [Part::Box] Box004  label="Cube001"
  Height = 1
  Length = 135
  Placement = pos=(0,-10,-10) rot=(0,0,1;0rad)
  Width = 20
FEATURE [Part::MultiFuse] Fusion011  label="Battery Holder"
  Placement = pos=(-67.5,-70,0) rot=(0,0,1;0rad)
  Shapes = -> [Cut035,Box004]
FEATURE [Part::MultiFuse] Fusion012  label="Battery Holder001"
  Placement = pos=(-67.5,-50,0) rot=(0,0,1;0rad)
  Shapes = -> [Cut035,Box004]
FEATURE [Part::MultiFuse] Fusion013  label="Battery Holder002"
  Placement = pos=(-67.5,-30,0) rot=(0,0,1;0rad)
  Shapes = -> [Cut035,Box004]
FEATURE [Part::MultiFuse] Fusion014  label="Battery holders s volume"
  Placement = pos=(0,0,-7) rot=(0,0,1;0rad)
  Shapes = -> [Fusion011,Fusion012,Fusion013]
